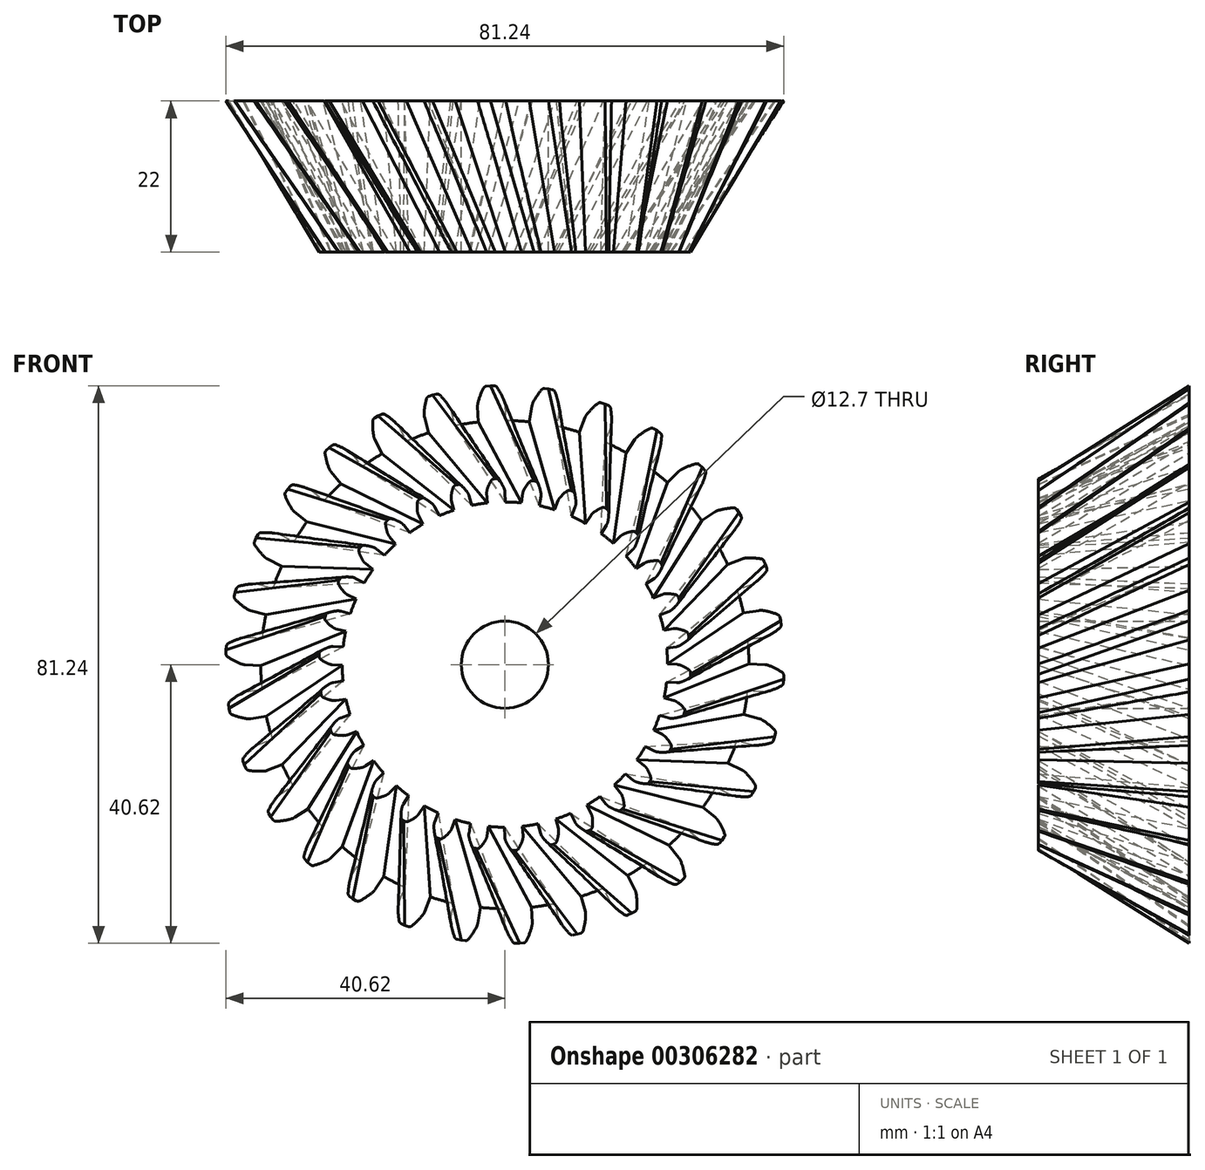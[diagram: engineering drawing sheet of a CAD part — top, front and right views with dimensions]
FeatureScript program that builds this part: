
annotation { "Feature Type Name" : "Feature", "Feature Type Description" : "" }
export const myFeature = defineFeature(function(context is Context, id is Id, definition is map)
    precondition{}
    {
        {
            var Q0;
            Q0=qCreatedBy(makeId("Front.planeOp"),FACE);
            cPlane(context, id + "F0", {"entities" : qUnion([Q0]), "cplaneType" : CPlaneType.OFFSET, "offset" : 22 * mm, "width" : 152.4 * mm, "height" : 152.4 * mm});
        }
        {
            var Q0;
            Q0=qCreatedBy(makeId("Front.planeOp"),FACE);
            var sketch = newSketch(context, id + "F1", { "sketchPlane" : qUnion([Q0])});
            skArc(sketch, "E0", {"start": v(-3.85, 35.35) * mm, "mid": v(-5.56, 35.12) * mm, "end": v(-7.26, 34.81) * mm});
            skArc(sketch, "E1.trimOffspring", {"start": v(-0.08, 38.33) * mm, "mid": v(-0.54, 39.4) * mm, "end": v(-1.12, 40.4) * mm});
            skLineSegment(sketch, "E2", {"start": v(-1.54, 40.62) * mm, "end": v(-2.13, 40.62) * mm});
            skLineSegment(sketch, "E3", {"start": v(0.01, 37.88) * mm, "end": v(0.13, 35.56) * mm});
            skLineSegment(sketch, "E4.MirrorCS", {"start": v(-2.7, 40.56) * mm, "end": v(-2.13, 40.62) * mm});
            skArc(sketch, "E5.MirrorCS", {"start": v(-3.93, 38.13) * mm, "mid": v(-3.58, 39.24) * mm, "end": v(-3.1, 40.3) * mm});
            skLineSegment(sketch, "E6.MirrorCS", {"start": v(-3.97, 37.67) * mm, "end": v(-3.85, 35.35) * mm});
            skPoint(sketch, "E7.visualSharp", {"position": v(-2.98, 40.53) * mm});
            skArc(sketch, "E7.filletArc", {"start": v(-2.7, 40.56) * mm, "mid": v(-2.94, 40.47) * mm, "end": v(-3.1, 40.3) * mm});
            skPoint(sketch, "E8.visualSharp", {"position": v(-1.28, 40.62) * mm});
            skArc(sketch, "E8.filletArc", {"start": v(-1.12, 40.4) * mm, "mid": v(-1.3, 40.56) * mm, "end": v(-1.54, 40.62) * mm});
            skPoint(sketch, "E9.visualSharp", {"position": v(-3.98, 37.9) * mm});
            skArc(sketch, "E9.filletArc", {"start": v(-3.93, 38.13) * mm, "mid": v(-3.97, 37.9) * mm, "end": v(-3.97, 37.67) * mm});
            skPoint(sketch, "E10.visualSharp", {"position": v(0, 38.1) * mm});
            skArc(sketch, "E10.filletArc", {"start": v(0.01, 37.88) * mm, "mid": v(-0.02, 38.1) * mm, "end": v(-0.08, 38.33) * mm});
            skLineSegment(sketch, "E11.1.0", {"start": v(-11.72, 36.02) * mm, "end": v(-11.12, 33.78) * mm});
            skPoint(sketch, "E11.1.1", {"position": v(-11.77, 36.24) * mm});
            skArc(sketch, "E11.1.2", {"start": v(-8.05, 37.48) * mm, "mid": v(-8.72, 38.42) * mm, "end": v(-9.5, 39.28) * mm});
            skArc(sketch, "E11.1.3", {"start": v(-11.77, 36.48) * mm, "mid": v(-11.66, 37.63) * mm, "end": v(-11.42, 38.76) * mm});
            skLineSegment(sketch, "E11.1.4", {"start": v(-9.96, 39.41) * mm, "end": v(-10.53, 39.29) * mm});
            skPoint(sketch, "E11.1.5", {"position": v(-11.34, 39.03) * mm});
            skPoint(sketch, "E11.1.6", {"position": v(-9.7, 39.47) * mm});
            skPoint(sketch, "E11.1.7", {"position": v(-7.92, 37.27) * mm});
            skLineSegment(sketch, "E11.1.8", {"start": v(-7.86, 37.05) * mm, "end": v(-7.26, 34.81) * mm});
            skLineSegment(sketch, "E11.1.9", {"start": v(-11.08, 39.1) * mm, "end": v(-10.53, 39.29) * mm});
            skArc(sketch, "E11.1.10", {"start": v(-11.08, 39.1) * mm, "mid": v(-11.3, 38.98) * mm, "end": v(-11.42, 38.76) * mm});
            skArc(sketch, "E11.1.11", {"start": v(-9.5, 39.28) * mm, "mid": v(-9.7, 39.4) * mm, "end": v(-9.96, 39.41) * mm});
            skArc(sketch, "E11.1.12", {"start": v(-11.77, 36.48) * mm, "mid": v(-11.76, 36.25) * mm, "end": v(-11.72, 36.02) * mm});
            skArc(sketch, "E11.1.13", {"start": v(-7.86, 37.05) * mm, "mid": v(-7.94, 37.27) * mm, "end": v(-8.05, 37.48) * mm});
            skLineSegment(sketch, "E11.2.0", {"start": v(-18.95, 32.8) * mm, "end": v(-17.9, 30.73) * mm});
            skPoint(sketch, "E11.2.1", {"position": v(-19.05, 33) * mm});
            skArc(sketch, "E11.2.2", {"start": v(-15.66, 34.99) * mm, "mid": v(-16.52, 35.77) * mm, "end": v(-17.45, 36.45) * mm});
            skArc(sketch, "E11.2.3", {"start": v(-19.1, 33.24) * mm, "mid": v(-19.23, 34.39) * mm, "end": v(-19.23, 35.54) * mm});
            skLineSegment(sketch, "E11.2.4", {"start": v(-17.93, 36.48) * mm, "end": v(-18.47, 36.24) * mm});
            skPoint(sketch, "E11.2.5", {"position": v(-19.2, 35.82) * mm});
            skPoint(sketch, "E11.2.6", {"position": v(-17.69, 36.59) * mm});
            skPoint(sketch, "E11.2.7", {"position": v(-15.5, 34.8) * mm});
            skLineSegment(sketch, "E11.2.8", {"start": v(-15.4, 34.6) * mm, "end": v(-14.34, 32.54) * mm});
            skLineSegment(sketch, "E11.2.9", {"start": v(-18.97, 35.95) * mm, "end": v(-18.47, 36.24) * mm});
            skArc(sketch, "E11.2.10", {"start": v(-18.97, 35.95) * mm, "mid": v(-19.15, 35.78) * mm, "end": v(-19.23, 35.54) * mm});
            skArc(sketch, "E11.2.11", {"start": v(-17.45, 36.45) * mm, "mid": v(-17.69, 36.52) * mm, "end": v(-17.93, 36.48) * mm});
            skArc(sketch, "E11.2.12", {"start": v(-19.1, 33.24) * mm, "mid": v(-19.04, 33.01) * mm, "end": v(-18.95, 32.8) * mm});
            skArc(sketch, "E11.2.13", {"start": v(-15.4, 34.6) * mm, "mid": v(-15.52, 34.8) * mm, "end": v(-15.66, 34.99) * mm});
            skLineSegment(sketch, "E11.3.0", {"start": v(-25.35, 28.14) * mm, "end": v(-23.9, 26.34) * mm});
            skPoint(sketch, "E11.3.1", {"position": v(-25.5, 28.31) * mm});
            skArc(sketch, "E11.3.2", {"start": v(-22.6, 30.96) * mm, "mid": v(-23.6, 31.55) * mm, "end": v(-24.65, 32.02) * mm});
            skArc(sketch, "E11.3.3", {"start": v(-25.59, 28.54) * mm, "mid": v(-25.96, 29.64) * mm, "end": v(-26.2, 30.77) * mm});
            skLineSegment(sketch, "E11.3.4", {"start": v(-25.13, 31.95) * mm, "end": v(-25.6, 31.61) * mm});
            skPoint(sketch, "E11.3.5", {"position": v(-26.23, 31.04) * mm});
            skPoint(sketch, "E11.3.6", {"position": v(-24.9, 32.11) * mm});
            skPoint(sketch, "E11.3.7", {"position": v(-22.4, 30.82) * mm});
            skLineSegment(sketch, "E11.3.8", {"start": v(-22.25, 30.65) * mm, "end": v(-20.8, 28.85) * mm});
            skLineSegment(sketch, "E11.3.9", {"start": v(-26.03, 31.22) * mm, "end": v(-25.6, 31.61) * mm});
            skArc(sketch, "E11.3.10", {"start": v(-26.03, 31.22) * mm, "mid": v(-26.17, 31.02) * mm, "end": v(-26.2, 30.77) * mm});
            skArc(sketch, "E11.3.11", {"start": v(-24.65, 32.02) * mm, "mid": v(-24.9, 32.05) * mm, "end": v(-25.13, 31.95) * mm});
            skArc(sketch, "E11.3.12", {"start": v(-25.59, 28.54) * mm, "mid": v(-25.49, 28.33) * mm, "end": v(-25.35, 28.14) * mm});
            skArc(sketch, "E11.3.13", {"start": v(-22.25, 30.65) * mm, "mid": v(-22.41, 30.82) * mm, "end": v(-22.6, 30.96) * mm});
            skLineSegment(sketch, "E11.4.0", {"start": v(-30.65, 22.25) * mm, "end": v(-28.85, 20.8) * mm});
            skPoint(sketch, "E11.4.1", {"position": v(-30.82, 22.4) * mm});
            skArc(sketch, "E11.4.2", {"start": v(-28.54, 25.59) * mm, "mid": v(-29.64, 25.96) * mm, "end": v(-30.77, 26.2) * mm});
            skArc(sketch, "E11.4.3", {"start": v(-30.96, 22.6) * mm, "mid": v(-31.55, 23.6) * mm, "end": v(-32.02, 24.65) * mm});
            skLineSegment(sketch, "E11.4.4", {"start": v(-31.22, 26.03) * mm, "end": v(-31.61, 25.6) * mm});
            skPoint(sketch, "E11.4.5", {"position": v(-32.11, 24.9) * mm});
            skPoint(sketch, "E11.4.6", {"position": v(-31.04, 26.23) * mm});
            skPoint(sketch, "E11.4.7", {"position": v(-28.31, 25.5) * mm});
            skLineSegment(sketch, "E11.4.8", {"start": v(-28.14, 25.35) * mm, "end": v(-26.34, 23.9) * mm});
            skLineSegment(sketch, "E11.4.9", {"start": v(-31.95, 25.13) * mm, "end": v(-31.61, 25.6) * mm});
            skArc(sketch, "E11.4.10", {"start": v(-31.95, 25.13) * mm, "mid": v(-32.05, 24.9) * mm, "end": v(-32.02, 24.65) * mm});
            skArc(sketch, "E11.4.11", {"start": v(-30.77, 26.2) * mm, "mid": v(-31.02, 26.17) * mm, "end": v(-31.22, 26.03) * mm});
            skArc(sketch, "E11.4.12", {"start": v(-30.96, 22.6) * mm, "mid": v(-30.82, 22.41) * mm, "end": v(-30.65, 22.25) * mm});
            skArc(sketch, "E11.4.13", {"start": v(-28.14, 25.35) * mm, "mid": v(-28.33, 25.49) * mm, "end": v(-28.54, 25.59) * mm});
            skLineSegment(sketch, "E11.5.0", {"start": v(-34.6, 15.4) * mm, "end": v(-32.54, 14.34) * mm});
            skPoint(sketch, "E11.5.1", {"position": v(-34.8, 15.5) * mm});
            skArc(sketch, "E11.5.2", {"start": v(-33.24, 19.1) * mm, "mid": v(-34.39, 19.23) * mm, "end": v(-35.54, 19.23) * mm});
            skArc(sketch, "E11.5.3", {"start": v(-34.99, 15.66) * mm, "mid": v(-35.77, 16.52) * mm, "end": v(-36.45, 17.45) * mm});
            skLineSegment(sketch, "E11.5.4", {"start": v(-35.95, 18.97) * mm, "end": v(-36.24, 18.47) * mm});
            skPoint(sketch, "E11.5.5", {"position": v(-36.59, 17.69) * mm});
            skPoint(sketch, "E11.5.6", {"position": v(-35.82, 19.2) * mm});
            skPoint(sketch, "E11.5.7", {"position": v(-33, 19.05) * mm});
            skLineSegment(sketch, "E11.5.8", {"start": v(-32.8, 18.95) * mm, "end": v(-30.73, 17.9) * mm});
            skLineSegment(sketch, "E11.5.9", {"start": v(-36.48, 17.93) * mm, "end": v(-36.24, 18.47) * mm});
            skArc(sketch, "E11.5.10", {"start": v(-36.48, 17.93) * mm, "mid": v(-36.52, 17.69) * mm, "end": v(-36.45, 17.45) * mm});
            skArc(sketch, "E11.5.11", {"start": v(-35.54, 19.23) * mm, "mid": v(-35.78, 19.15) * mm, "end": v(-35.95, 18.97) * mm});
            skArc(sketch, "E11.5.12", {"start": v(-34.99, 15.66) * mm, "mid": v(-34.8, 15.52) * mm, "end": v(-34.6, 15.4) * mm});
            skArc(sketch, "E11.5.13", {"start": v(-32.8, 18.95) * mm, "mid": v(-33.01, 19.04) * mm, "end": v(-33.24, 19.1) * mm});
            skLineSegment(sketch, "E11.6.0", {"start": v(-37.05, 7.86) * mm, "end": v(-34.81, 7.26) * mm});
            skPoint(sketch, "E11.6.1", {"position": v(-37.27, 7.92) * mm});
            skArc(sketch, "E11.6.2", {"start": v(-36.48, 11.77) * mm, "mid": v(-37.63, 11.66) * mm, "end": v(-38.76, 11.42) * mm});
            skArc(sketch, "E11.6.3", {"start": v(-37.48, 8.05) * mm, "mid": v(-38.42, 8.72) * mm, "end": v(-39.28, 9.5) * mm});
            skLineSegment(sketch, "E11.6.4", {"start": v(-39.1, 11.08) * mm, "end": v(-39.29, 10.53) * mm});
            skPoint(sketch, "E11.6.5", {"position": v(-39.47, 9.7) * mm});
            skPoint(sketch, "E11.6.6", {"position": v(-39.03, 11.34) * mm});
            skPoint(sketch, "E11.6.7", {"position": v(-36.24, 11.77) * mm});
            skLineSegment(sketch, "E11.6.8", {"start": v(-36.02, 11.72) * mm, "end": v(-33.78, 11.12) * mm});
            skLineSegment(sketch, "E11.6.9", {"start": v(-39.41, 9.96) * mm, "end": v(-39.29, 10.53) * mm});
            skArc(sketch, "E11.6.10", {"start": v(-39.41, 9.96) * mm, "mid": v(-39.4, 9.7) * mm, "end": v(-39.28, 9.5) * mm});
            skArc(sketch, "E11.6.11", {"start": v(-38.76, 11.42) * mm, "mid": v(-38.98, 11.3) * mm, "end": v(-39.1, 11.08) * mm});
            skArc(sketch, "E11.6.12", {"start": v(-37.48, 8.05) * mm, "mid": v(-37.27, 7.94) * mm, "end": v(-37.05, 7.86) * mm});
            skArc(sketch, "E11.6.13", {"start": v(-36.02, 11.72) * mm, "mid": v(-36.25, 11.76) * mm, "end": v(-36.48, 11.77) * mm});
            skLineSegment(sketch, "E11.7.0", {"start": v(-37.88, -0.01) * mm, "end": v(-35.56, -0.13) * mm});
            skPoint(sketch, "E11.7.1", {"position": v(-38.1, 0) * mm});
            skArc(sketch, "E11.7.2", {"start": v(-38.13, 3.93) * mm, "mid": v(-39.24, 3.58) * mm, "end": v(-40.3, 3.1) * mm});
            skArc(sketch, "E11.7.3", {"start": v(-38.33, 0.08) * mm, "mid": v(-39.4, 0.54) * mm, "end": v(-40.4, 1.12) * mm});
            skLineSegment(sketch, "E11.7.4", {"start": v(-40.56, 2.7) * mm, "end": v(-40.62, 2.13) * mm});
            skPoint(sketch, "E11.7.5", {"position": v(-40.62, 1.28) * mm});
            skPoint(sketch, "E11.7.6", {"position": v(-40.53, 2.98) * mm});
            skPoint(sketch, "E11.7.7", {"position": v(-37.9, 3.98) * mm});
            skLineSegment(sketch, "E11.7.8", {"start": v(-37.67, 3.97) * mm, "end": v(-35.35, 3.85) * mm});
            skLineSegment(sketch, "E11.7.9", {"start": v(-40.62, 1.54) * mm, "end": v(-40.62, 2.13) * mm});
            skArc(sketch, "E11.7.10", {"start": v(-40.62, 1.54) * mm, "mid": v(-40.56, 1.3) * mm, "end": v(-40.4, 1.12) * mm});
            skArc(sketch, "E11.7.11", {"start": v(-40.3, 3.1) * mm, "mid": v(-40.47, 2.94) * mm, "end": v(-40.56, 2.7) * mm});
            skArc(sketch, "E11.7.12", {"start": v(-38.33, 0.08) * mm, "mid": v(-38.1, 0.02) * mm, "end": v(-37.88, -0.01) * mm});
            skArc(sketch, "E11.7.13", {"start": v(-37.67, 3.97) * mm, "mid": v(-37.9, 3.97) * mm, "end": v(-38.13, 3.93) * mm});
            skLineSegment(sketch, "E11.8.0", {"start": v(-37.05, -7.89) * mm, "end": v(-34.76, -7.52) * mm});
            skPoint(sketch, "E11.8.1", {"position": v(-37.27, -7.92) * mm});
            skArc(sketch, "E11.8.2", {"start": v(-38.11, -4.09) * mm, "mid": v(-39.12, -4.65) * mm, "end": v(-40.06, -5.34) * mm});
            skArc(sketch, "E11.8.3", {"start": v(-37.51, -7.9) * mm, "mid": v(-38.65, -7.66) * mm, "end": v(-39.74, -7.3) * mm});
            skLineSegment(sketch, "E11.8.4", {"start": v(-40.24, -5.78) * mm, "end": v(-40.17, -6.36) * mm});
            skPoint(sketch, "E11.8.5", {"position": v(-40, -7.2) * mm});
            skPoint(sketch, "E11.8.6", {"position": v(-40.26, -5.52) * mm});
            skPoint(sketch, "E11.8.7", {"position": v(-37.9, -3.98) * mm});
            skLineSegment(sketch, "E11.8.8", {"start": v(-37.67, -3.95) * mm, "end": v(-35.38, -3.58) * mm});
            skLineSegment(sketch, "E11.8.9", {"start": v(-40.05, -6.93) * mm, "end": v(-40.17, -6.36) * mm});
            skArc(sketch, "E11.8.10", {"start": v(-40.05, -6.93) * mm, "mid": v(-39.94, -7.16) * mm, "end": v(-39.74, -7.3) * mm});
            skArc(sketch, "E11.8.11", {"start": v(-40.06, -5.34) * mm, "mid": v(-40.2, -5.54) * mm, "end": v(-40.24, -5.78) * mm});
            skArc(sketch, "E11.8.12", {"start": v(-37.51, -7.9) * mm, "mid": v(-37.28, -7.9) * mm, "end": v(-37.05, -7.89) * mm});
            skArc(sketch, "E11.8.13", {"start": v(-37.67, -3.95) * mm, "mid": v(-37.9, -4) * mm, "end": v(-38.11, -4.09) * mm});
            skLineSegment(sketch, "E11.9.0", {"start": v(-34.6, -15.42) * mm, "end": v(-32.43, -14.59) * mm});
            skPoint(sketch, "E11.9.1", {"position": v(-34.8, -15.5) * mm});
            skArc(sketch, "E11.9.2", {"start": v(-36.43, -11.92) * mm, "mid": v(-37.3, -12.69) * mm, "end": v(-38.07, -13.55) * mm});
            skArc(sketch, "E11.9.3", {"start": v(-35.05, -15.52) * mm, "mid": v(-36.2, -15.53) * mm, "end": v(-37.36, -15.4) * mm});
            skLineSegment(sketch, "E11.9.4", {"start": v(-38.15, -14.02) * mm, "end": v(-37.97, -14.58) * mm});
            skPoint(sketch, "E11.9.5", {"position": v(-37.63, -15.35) * mm});
            skPoint(sketch, "E11.9.6", {"position": v(-38.24, -13.77) * mm});
            skPoint(sketch, "E11.9.7", {"position": v(-36.24, -11.77) * mm});
            skLineSegment(sketch, "E11.9.8", {"start": v(-36.03, -11.7) * mm, "end": v(-33.86, -10.86) * mm});
            skLineSegment(sketch, "E11.9.9", {"start": v(-37.74, -15.11) * mm, "end": v(-37.97, -14.58) * mm});
            skArc(sketch, "E11.9.10", {"start": v(-37.74, -15.11) * mm, "mid": v(-37.58, -15.3) * mm, "end": v(-37.36, -15.4) * mm});
            skArc(sketch, "E11.9.11", {"start": v(-38.07, -13.55) * mm, "mid": v(-38.17, -13.77) * mm, "end": v(-38.15, -14.02) * mm});
            skArc(sketch, "E11.9.12", {"start": v(-35.05, -15.52) * mm, "mid": v(-34.82, -15.48) * mm, "end": v(-34.6, -15.42) * mm});
            skArc(sketch, "E11.9.13", {"start": v(-36.03, -11.7) * mm, "mid": v(-36.24, -11.8) * mm, "end": v(-36.43, -11.92) * mm});
            skLineSegment(sketch, "E11.10.0", {"start": v(-30.64, -22.27) * mm, "end": v(-28.7, -21) * mm});
            skPoint(sketch, "E11.10.1", {"position": v(-30.82, -22.4) * mm});
            skArc(sketch, "E11.10.2", {"start": v(-33.16, -19.24) * mm, "mid": v(-33.85, -20.16) * mm, "end": v(-34.42, -21.17) * mm});
            skArc(sketch, "E11.10.3", {"start": v(-31.06, -22.47) * mm, "mid": v(-32.19, -22.72) * mm, "end": v(-33.34, -22.84) * mm});
            skLineSegment(sketch, "E11.10.4", {"start": v(-34.4, -21.65) * mm, "end": v(-34.11, -22.15) * mm});
            skPoint(sketch, "E11.10.5", {"position": v(-33.61, -22.84) * mm});
            skPoint(sketch, "E11.10.6", {"position": v(-34.54, -21.42) * mm});
            skPoint(sketch, "E11.10.7", {"position": v(-33, -19.05) * mm});
            skLineSegment(sketch, "E11.10.8", {"start": v(-32.8, -18.93) * mm, "end": v(-30.86, -17.66) * mm});
            skLineSegment(sketch, "E11.10.9", {"start": v(-33.77, -22.63) * mm, "end": v(-34.11, -22.15) * mm});
            skArc(sketch, "E11.10.10", {"start": v(-33.77, -22.63) * mm, "mid": v(-33.58, -22.78) * mm, "end": v(-33.34, -22.84) * mm});
            skArc(sketch, "E11.10.11", {"start": v(-34.42, -21.17) * mm, "mid": v(-34.47, -21.41) * mm, "end": v(-34.4, -21.65) * mm});
            skArc(sketch, "E11.10.12", {"start": v(-31.06, -22.47) * mm, "mid": v(-30.84, -22.38) * mm, "end": v(-30.64, -22.27) * mm});
            skArc(sketch, "E11.10.13", {"start": v(-32.8, -18.93) * mm, "mid": v(-33, -19.07) * mm, "end": v(-33.16, -19.24) * mm});
            skLineSegment(sketch, "E11.11.0", {"start": v(-25.34, -28.16) * mm, "end": v(-23.7, -26.52) * mm});
            skPoint(sketch, "E11.11.1", {"position": v(-25.5, -28.31) * mm});
            skArc(sketch, "E11.11.2", {"start": v(-28.43, -25.7) * mm, "mid": v(-28.92, -26.76) * mm, "end": v(-29.27, -27.86) * mm});
            skArc(sketch, "E11.11.3", {"start": v(-25.7, -28.43) * mm, "mid": v(-26.76, -28.92) * mm, "end": v(-27.86, -29.27) * mm});
            skLineSegment(sketch, "E11.11.4", {"start": v(-29.15, -28.33) * mm, "end": v(-28.76, -28.76) * mm});
            skPoint(sketch, "E11.11.5", {"position": v(-28.13, -29.33) * mm});
            skPoint(sketch, "E11.11.6", {"position": v(-29.33, -28.13) * mm});
            skPoint(sketch, "E11.11.7", {"position": v(-28.31, -25.5) * mm});
            skLineSegment(sketch, "E11.11.8", {"start": v(-28.16, -25.34) * mm, "end": v(-26.52, -23.7) * mm});
            skLineSegment(sketch, "E11.11.9", {"start": v(-28.33, -29.15) * mm, "end": v(-28.76, -28.76) * mm});
            skArc(sketch, "E11.11.10", {"start": v(-28.33, -29.15) * mm, "mid": v(-28.1, -29.27) * mm, "end": v(-27.86, -29.27) * mm});
            skArc(sketch, "E11.11.11", {"start": v(-29.27, -27.86) * mm, "mid": v(-29.27, -28.1) * mm, "end": v(-29.15, -28.33) * mm});
            skArc(sketch, "E11.11.12", {"start": v(-25.7, -28.43) * mm, "mid": v(-25.51, -28.3) * mm, "end": v(-25.34, -28.16) * mm});
            skArc(sketch, "E11.11.13", {"start": v(-28.16, -25.34) * mm, "mid": v(-28.3, -25.51) * mm, "end": v(-28.43, -25.7) * mm});
            skLineSegment(sketch, "E11.12.0", {"start": v(-18.93, -32.8) * mm, "end": v(-17.66, -30.86) * mm});
            skPoint(sketch, "E11.12.1", {"position": v(-19.05, -33) * mm});
            skArc(sketch, "E11.12.2", {"start": v(-22.47, -31.06) * mm, "mid": v(-22.72, -32.19) * mm, "end": v(-22.84, -33.34) * mm});
            skArc(sketch, "E11.12.3", {"start": v(-19.24, -33.16) * mm, "mid": v(-20.16, -33.85) * mm, "end": v(-21.17, -34.42) * mm});
            skLineSegment(sketch, "E11.12.4", {"start": v(-22.63, -33.77) * mm, "end": v(-22.15, -34.11) * mm});
            skPoint(sketch, "E11.12.5", {"position": v(-21.42, -34.54) * mm});
            skPoint(sketch, "E11.12.6", {"position": v(-22.84, -33.61) * mm});
            skPoint(sketch, "E11.12.7", {"position": v(-22.4, -30.82) * mm});
            skLineSegment(sketch, "E11.12.8", {"start": v(-22.27, -30.64) * mm, "end": v(-21, -28.7) * mm});
            skLineSegment(sketch, "E11.12.9", {"start": v(-21.65, -34.4) * mm, "end": v(-22.15, -34.11) * mm});
            skArc(sketch, "E11.12.10", {"start": v(-21.65, -34.4) * mm, "mid": v(-21.41, -34.47) * mm, "end": v(-21.17, -34.42) * mm});
            skArc(sketch, "E11.12.11", {"start": v(-22.84, -33.34) * mm, "mid": v(-22.78, -33.58) * mm, "end": v(-22.63, -33.77) * mm});
            skArc(sketch, "E11.12.12", {"start": v(-19.24, -33.16) * mm, "mid": v(-19.07, -33) * mm, "end": v(-18.93, -32.8) * mm});
            skArc(sketch, "E11.12.13", {"start": v(-22.27, -30.64) * mm, "mid": v(-22.38, -30.84) * mm, "end": v(-22.47, -31.06) * mm});
            skLineSegment(sketch, "E11.13.0", {"start": v(-11.7, -36.03) * mm, "end": v(-10.86, -33.86) * mm});
            skPoint(sketch, "E11.13.1", {"position": v(-11.77, -36.24) * mm});
            skArc(sketch, "E11.13.2", {"start": v(-15.52, -35.05) * mm, "mid": v(-15.53, -36.2) * mm, "end": v(-15.4, -37.36) * mm});
            skArc(sketch, "E11.13.3", {"start": v(-11.92, -36.43) * mm, "mid": v(-12.69, -37.3) * mm, "end": v(-13.55, -38.07) * mm});
            skLineSegment(sketch, "E11.13.4", {"start": v(-15.11, -37.74) * mm, "end": v(-14.58, -37.97) * mm});
            skPoint(sketch, "E11.13.5", {"position": v(-13.77, -38.24) * mm});
            skPoint(sketch, "E11.13.6", {"position": v(-15.35, -37.63) * mm});
            skPoint(sketch, "E11.13.7", {"position": v(-15.5, -34.8) * mm});
            skLineSegment(sketch, "E11.13.8", {"start": v(-15.42, -34.6) * mm, "end": v(-14.59, -32.43) * mm});
            skLineSegment(sketch, "E11.13.9", {"start": v(-14.02, -38.15) * mm, "end": v(-14.58, -37.97) * mm});
            skArc(sketch, "E11.13.10", {"start": v(-14.02, -38.15) * mm, "mid": v(-13.77, -38.17) * mm, "end": v(-13.55, -38.07) * mm});
            skArc(sketch, "E11.13.11", {"start": v(-15.4, -37.36) * mm, "mid": v(-15.3, -37.58) * mm, "end": v(-15.11, -37.74) * mm});
            skArc(sketch, "E11.13.12", {"start": v(-11.92, -36.43) * mm, "mid": v(-11.8, -36.24) * mm, "end": v(-11.7, -36.03) * mm});
            skArc(sketch, "E11.13.13", {"start": v(-15.42, -34.6) * mm, "mid": v(-15.48, -34.82) * mm, "end": v(-15.52, -35.05) * mm});
            skLineSegment(sketch, "E11.14.0", {"start": v(-3.95, -37.67) * mm, "end": v(-3.58, -35.38) * mm});
            skPoint(sketch, "E11.14.1", {"position": v(-3.98, -37.9) * mm});
            skArc(sketch, "E11.14.2", {"start": v(-7.9, -37.51) * mm, "mid": v(-7.66, -38.65) * mm, "end": v(-7.3, -39.74) * mm});
            skArc(sketch, "E11.14.3", {"start": v(-4.09, -38.11) * mm, "mid": v(-4.65, -39.12) * mm, "end": v(-5.34, -40.06) * mm});
            skLineSegment(sketch, "E11.14.4", {"start": v(-6.93, -40.05) * mm, "end": v(-6.36, -40.17) * mm});
            skPoint(sketch, "E11.14.5", {"position": v(-5.52, -40.26) * mm});
            skPoint(sketch, "E11.14.6", {"position": v(-7.2, -40) * mm});
            skPoint(sketch, "E11.14.7", {"position": v(-7.92, -37.27) * mm});
            skLineSegment(sketch, "E11.14.8", {"start": v(-7.89, -37.05) * mm, "end": v(-7.52, -34.76) * mm});
            skLineSegment(sketch, "E11.14.9", {"start": v(-5.78, -40.24) * mm, "end": v(-6.36, -40.17) * mm});
            skArc(sketch, "E11.14.10", {"start": v(-5.78, -40.24) * mm, "mid": v(-5.54, -40.2) * mm, "end": v(-5.34, -40.06) * mm});
            skArc(sketch, "E11.14.11", {"start": v(-7.3, -39.74) * mm, "mid": v(-7.16, -39.94) * mm, "end": v(-6.93, -40.05) * mm});
            skArc(sketch, "E11.14.12", {"start": v(-4.09, -38.11) * mm, "mid": v(-4, -37.9) * mm, "end": v(-3.95, -37.67) * mm});
            skArc(sketch, "E11.14.13", {"start": v(-7.89, -37.05) * mm, "mid": v(-7.9, -37.28) * mm, "end": v(-7.9, -37.51) * mm});
            skLineSegment(sketch, "E11.15.0", {"start": v(3.97, -37.67) * mm, "end": v(3.85, -35.35) * mm});
            skPoint(sketch, "E11.15.1", {"position": v(3.98, -37.9) * mm});
            skArc(sketch, "E11.15.2", {"start": v(0.08, -38.33) * mm, "mid": v(0.54, -39.4) * mm, "end": v(1.12, -40.4) * mm});
            skArc(sketch, "E11.15.3", {"start": v(3.93, -38.13) * mm, "mid": v(3.58, -39.24) * mm, "end": v(3.1, -40.3) * mm});
            skLineSegment(sketch, "E11.15.4", {"start": v(1.54, -40.62) * mm, "end": v(2.13, -40.62) * mm});
            skPoint(sketch, "E11.15.5", {"position": v(2.98, -40.53) * mm});
            skPoint(sketch, "E11.15.6", {"position": v(1.28, -40.62) * mm});
            skPoint(sketch, "E11.15.7", {"position": v(0, -38.1) * mm});
            skLineSegment(sketch, "E11.15.8", {"start": v(-0.01, -37.88) * mm, "end": v(-0.13, -35.56) * mm});
            skLineSegment(sketch, "E11.15.9", {"start": v(2.7, -40.56) * mm, "end": v(2.13, -40.62) * mm});
            skArc(sketch, "E11.15.10", {"start": v(2.7, -40.56) * mm, "mid": v(2.94, -40.47) * mm, "end": v(3.1, -40.3) * mm});
            skArc(sketch, "E11.15.11", {"start": v(1.12, -40.4) * mm, "mid": v(1.3, -40.56) * mm, "end": v(1.54, -40.62) * mm});
            skArc(sketch, "E11.15.12", {"start": v(3.93, -38.13) * mm, "mid": v(3.97, -37.9) * mm, "end": v(3.97, -37.67) * mm});
            skArc(sketch, "E11.15.13", {"start": v(-0.01, -37.88) * mm, "mid": v(0.02, -38.1) * mm, "end": v(0.08, -38.33) * mm});
            skLineSegment(sketch, "E11.16.0", {"start": v(11.72, -36.02) * mm, "end": v(11.12, -33.78) * mm});
            skPoint(sketch, "E11.16.1", {"position": v(11.77, -36.24) * mm});
            skArc(sketch, "E11.16.2", {"start": v(8.05, -37.48) * mm, "mid": v(8.72, -38.42) * mm, "end": v(9.5, -39.28) * mm});
            skArc(sketch, "E11.16.3", {"start": v(11.77, -36.48) * mm, "mid": v(11.66, -37.63) * mm, "end": v(11.42, -38.76) * mm});
            skLineSegment(sketch, "E11.16.4", {"start": v(9.96, -39.41) * mm, "end": v(10.53, -39.29) * mm});
            skPoint(sketch, "E11.16.5", {"position": v(11.34, -39.03) * mm});
            skPoint(sketch, "E11.16.6", {"position": v(9.7, -39.47) * mm});
            skPoint(sketch, "E11.16.7", {"position": v(7.92, -37.27) * mm});
            skLineSegment(sketch, "E11.16.8", {"start": v(7.86, -37.05) * mm, "end": v(7.26, -34.81) * mm});
            skLineSegment(sketch, "E11.16.9", {"start": v(11.08, -39.1) * mm, "end": v(10.53, -39.29) * mm});
            skArc(sketch, "E11.16.10", {"start": v(11.08, -39.1) * mm, "mid": v(11.3, -38.98) * mm, "end": v(11.42, -38.76) * mm});
            skArc(sketch, "E11.16.11", {"start": v(9.5, -39.28) * mm, "mid": v(9.7, -39.4) * mm, "end": v(9.96, -39.41) * mm});
            skArc(sketch, "E11.16.12", {"start": v(11.77, -36.48) * mm, "mid": v(11.76, -36.25) * mm, "end": v(11.72, -36.02) * mm});
            skArc(sketch, "E11.16.13", {"start": v(7.86, -37.05) * mm, "mid": v(7.94, -37.27) * mm, "end": v(8.05, -37.48) * mm});
            skLineSegment(sketch, "E11.17.0", {"start": v(18.95, -32.8) * mm, "end": v(17.9, -30.73) * mm});
            skPoint(sketch, "E11.17.1", {"position": v(19.05, -33) * mm});
            skArc(sketch, "E11.17.2", {"start": v(15.66, -34.99) * mm, "mid": v(16.52, -35.77) * mm, "end": v(17.45, -36.45) * mm});
            skArc(sketch, "E11.17.3", {"start": v(19.1, -33.24) * mm, "mid": v(19.23, -34.39) * mm, "end": v(19.23, -35.54) * mm});
            skLineSegment(sketch, "E11.17.4", {"start": v(17.93, -36.48) * mm, "end": v(18.47, -36.24) * mm});
            skPoint(sketch, "E11.17.5", {"position": v(19.2, -35.82) * mm});
            skPoint(sketch, "E11.17.6", {"position": v(17.69, -36.59) * mm});
            skPoint(sketch, "E11.17.7", {"position": v(15.5, -34.8) * mm});
            skLineSegment(sketch, "E11.17.8", {"start": v(15.4, -34.6) * mm, "end": v(14.34, -32.54) * mm});
            skLineSegment(sketch, "E11.17.9", {"start": v(18.97, -35.95) * mm, "end": v(18.47, -36.24) * mm});
            skArc(sketch, "E11.17.10", {"start": v(18.97, -35.95) * mm, "mid": v(19.15, -35.78) * mm, "end": v(19.23, -35.54) * mm});
            skArc(sketch, "E11.17.11", {"start": v(17.45, -36.45) * mm, "mid": v(17.69, -36.52) * mm, "end": v(17.93, -36.48) * mm});
            skArc(sketch, "E11.17.12", {"start": v(19.1, -33.24) * mm, "mid": v(19.04, -33.01) * mm, "end": v(18.95, -32.8) * mm});
            skArc(sketch, "E11.17.13", {"start": v(15.4, -34.6) * mm, "mid": v(15.52, -34.8) * mm, "end": v(15.66, -34.99) * mm});
            skLineSegment(sketch, "E11.18.0", {"start": v(25.35, -28.14) * mm, "end": v(23.9, -26.34) * mm});
            skPoint(sketch, "E11.18.1", {"position": v(25.5, -28.31) * mm});
            skArc(sketch, "E11.18.2", {"start": v(22.6, -30.96) * mm, "mid": v(23.6, -31.55) * mm, "end": v(24.65, -32.02) * mm});
            skArc(sketch, "E11.18.3", {"start": v(25.59, -28.54) * mm, "mid": v(25.96, -29.64) * mm, "end": v(26.2, -30.77) * mm});
            skLineSegment(sketch, "E11.18.4", {"start": v(25.13, -31.95) * mm, "end": v(25.6, -31.61) * mm});
            skPoint(sketch, "E11.18.5", {"position": v(26.23, -31.04) * mm});
            skPoint(sketch, "E11.18.6", {"position": v(24.9, -32.11) * mm});
            skPoint(sketch, "E11.18.7", {"position": v(22.4, -30.82) * mm});
            skLineSegment(sketch, "E11.18.8", {"start": v(22.25, -30.65) * mm, "end": v(20.8, -28.85) * mm});
            skLineSegment(sketch, "E11.18.9", {"start": v(26.03, -31.22) * mm, "end": v(25.6, -31.61) * mm});
            skArc(sketch, "E11.18.10", {"start": v(26.03, -31.22) * mm, "mid": v(26.17, -31.02) * mm, "end": v(26.2, -30.77) * mm});
            skArc(sketch, "E11.18.11", {"start": v(24.65, -32.02) * mm, "mid": v(24.9, -32.05) * mm, "end": v(25.13, -31.95) * mm});
            skArc(sketch, "E11.18.12", {"start": v(25.59, -28.54) * mm, "mid": v(25.49, -28.33) * mm, "end": v(25.35, -28.14) * mm});
            skArc(sketch, "E11.18.13", {"start": v(22.25, -30.65) * mm, "mid": v(22.41, -30.82) * mm, "end": v(22.6, -30.96) * mm});
            skLineSegment(sketch, "E11.19.0", {"start": v(30.65, -22.25) * mm, "end": v(28.85, -20.8) * mm});
            skPoint(sketch, "E11.19.1", {"position": v(30.82, -22.4) * mm});
            skArc(sketch, "E11.19.2", {"start": v(28.54, -25.59) * mm, "mid": v(29.64, -25.96) * mm, "end": v(30.77, -26.2) * mm});
            skArc(sketch, "E11.19.3", {"start": v(30.96, -22.6) * mm, "mid": v(31.55, -23.6) * mm, "end": v(32.02, -24.65) * mm});
            skLineSegment(sketch, "E11.19.4", {"start": v(31.22, -26.03) * mm, "end": v(31.61, -25.6) * mm});
            skPoint(sketch, "E11.19.5", {"position": v(32.11, -24.9) * mm});
            skPoint(sketch, "E11.19.6", {"position": v(31.04, -26.23) * mm});
            skPoint(sketch, "E11.19.7", {"position": v(28.31, -25.5) * mm});
            skLineSegment(sketch, "E11.19.8", {"start": v(28.14, -25.35) * mm, "end": v(26.34, -23.9) * mm});
            skLineSegment(sketch, "E11.19.9", {"start": v(31.95, -25.13) * mm, "end": v(31.61, -25.6) * mm});
            skArc(sketch, "E11.19.10", {"start": v(31.95, -25.13) * mm, "mid": v(32.05, -24.9) * mm, "end": v(32.02, -24.65) * mm});
            skArc(sketch, "E11.19.11", {"start": v(30.77, -26.2) * mm, "mid": v(31.02, -26.17) * mm, "end": v(31.22, -26.03) * mm});
            skArc(sketch, "E11.19.12", {"start": v(30.96, -22.6) * mm, "mid": v(30.82, -22.41) * mm, "end": v(30.65, -22.25) * mm});
            skArc(sketch, "E11.19.13", {"start": v(28.14, -25.35) * mm, "mid": v(28.33, -25.49) * mm, "end": v(28.54, -25.59) * mm});
            skLineSegment(sketch, "E11.20.0", {"start": v(34.6, -15.4) * mm, "end": v(32.54, -14.34) * mm});
            skPoint(sketch, "E11.20.1", {"position": v(34.8, -15.5) * mm});
            skArc(sketch, "E11.20.2", {"start": v(33.24, -19.1) * mm, "mid": v(34.39, -19.23) * mm, "end": v(35.54, -19.23) * mm});
            skArc(sketch, "E11.20.3", {"start": v(34.99, -15.66) * mm, "mid": v(35.77, -16.52) * mm, "end": v(36.45, -17.45) * mm});
            skLineSegment(sketch, "E11.20.4", {"start": v(35.95, -18.97) * mm, "end": v(36.24, -18.47) * mm});
            skPoint(sketch, "E11.20.5", {"position": v(36.59, -17.69) * mm});
            skPoint(sketch, "E11.20.6", {"position": v(35.82, -19.2) * mm});
            skPoint(sketch, "E11.20.7", {"position": v(33, -19.05) * mm});
            skLineSegment(sketch, "E11.20.8", {"start": v(32.8, -18.95) * mm, "end": v(30.73, -17.9) * mm});
            skLineSegment(sketch, "E11.20.9", {"start": v(36.48, -17.93) * mm, "end": v(36.24, -18.47) * mm});
            skArc(sketch, "E11.20.10", {"start": v(36.48, -17.93) * mm, "mid": v(36.52, -17.69) * mm, "end": v(36.45, -17.45) * mm});
            skArc(sketch, "E11.20.11", {"start": v(35.54, -19.23) * mm, "mid": v(35.78, -19.15) * mm, "end": v(35.95, -18.97) * mm});
            skArc(sketch, "E11.20.12", {"start": v(34.99, -15.66) * mm, "mid": v(34.8, -15.52) * mm, "end": v(34.6, -15.4) * mm});
            skArc(sketch, "E11.20.13", {"start": v(32.8, -18.95) * mm, "mid": v(33.01, -19.04) * mm, "end": v(33.24, -19.1) * mm});
            skLineSegment(sketch, "E11.21.0", {"start": v(37.05, -7.86) * mm, "end": v(34.81, -7.26) * mm});
            skPoint(sketch, "E11.21.1", {"position": v(37.27, -7.92) * mm});
            skArc(sketch, "E11.21.2", {"start": v(36.48, -11.77) * mm, "mid": v(37.63, -11.66) * mm, "end": v(38.76, -11.42) * mm});
            skArc(sketch, "E11.21.3", {"start": v(37.48, -8.05) * mm, "mid": v(38.42, -8.72) * mm, "end": v(39.28, -9.5) * mm});
            skLineSegment(sketch, "E11.21.4", {"start": v(39.1, -11.08) * mm, "end": v(39.29, -10.53) * mm});
            skPoint(sketch, "E11.21.5", {"position": v(39.47, -9.7) * mm});
            skPoint(sketch, "E11.21.6", {"position": v(39.03, -11.34) * mm});
            skPoint(sketch, "E11.21.7", {"position": v(36.24, -11.77) * mm});
            skLineSegment(sketch, "E11.21.8", {"start": v(36.02, -11.72) * mm, "end": v(33.78, -11.12) * mm});
            skLineSegment(sketch, "E11.21.9", {"start": v(39.41, -9.96) * mm, "end": v(39.29, -10.53) * mm});
            skArc(sketch, "E11.21.10", {"start": v(39.41, -9.96) * mm, "mid": v(39.4, -9.7) * mm, "end": v(39.28, -9.5) * mm});
            skArc(sketch, "E11.21.11", {"start": v(38.76, -11.42) * mm, "mid": v(38.98, -11.3) * mm, "end": v(39.1, -11.08) * mm});
            skArc(sketch, "E11.21.12", {"start": v(37.48, -8.05) * mm, "mid": v(37.27, -7.94) * mm, "end": v(37.05, -7.86) * mm});
            skArc(sketch, "E11.21.13", {"start": v(36.02, -11.72) * mm, "mid": v(36.25, -11.76) * mm, "end": v(36.48, -11.77) * mm});
            skLineSegment(sketch, "E11.22.0", {"start": v(37.88, 0.01) * mm, "end": v(35.56, 0.13) * mm});
            skPoint(sketch, "E11.22.1", {"position": v(38.1, 0) * mm});
            skArc(sketch, "E11.22.2", {"start": v(38.13, -3.93) * mm, "mid": v(39.24, -3.58) * mm, "end": v(40.3, -3.1) * mm});
            skArc(sketch, "E11.22.3", {"start": v(38.33, -0.08) * mm, "mid": v(39.4, -0.54) * mm, "end": v(40.4, -1.12) * mm});
            skLineSegment(sketch, "E11.22.4", {"start": v(40.56, -2.7) * mm, "end": v(40.62, -2.13) * mm});
            skPoint(sketch, "E11.22.5", {"position": v(40.62, -1.28) * mm});
            skPoint(sketch, "E11.22.6", {"position": v(40.53, -2.98) * mm});
            skPoint(sketch, "E11.22.7", {"position": v(37.9, -3.98) * mm});
            skLineSegment(sketch, "E11.22.8", {"start": v(37.67, -3.97) * mm, "end": v(35.35, -3.85) * mm});
            skLineSegment(sketch, "E11.22.9", {"start": v(40.62, -1.54) * mm, "end": v(40.62, -2.13) * mm});
            skArc(sketch, "E11.22.10", {"start": v(40.62, -1.54) * mm, "mid": v(40.56, -1.3) * mm, "end": v(40.4, -1.12) * mm});
            skArc(sketch, "E11.22.11", {"start": v(40.3, -3.1) * mm, "mid": v(40.47, -2.94) * mm, "end": v(40.56, -2.7) * mm});
            skArc(sketch, "E11.22.12", {"start": v(38.33, -0.08) * mm, "mid": v(38.1, -0.02) * mm, "end": v(37.88, 0.01) * mm});
            skArc(sketch, "E11.22.13", {"start": v(37.67, -3.97) * mm, "mid": v(37.9, -3.97) * mm, "end": v(38.13, -3.93) * mm});
            skLineSegment(sketch, "E11.23.0", {"start": v(37.05, 7.89) * mm, "end": v(34.76, 7.52) * mm});
            skPoint(sketch, "E11.23.1", {"position": v(37.27, 7.92) * mm});
            skArc(sketch, "E11.23.2", {"start": v(38.11, 4.09) * mm, "mid": v(39.12, 4.65) * mm, "end": v(40.06, 5.34) * mm});
            skArc(sketch, "E11.23.3", {"start": v(37.51, 7.9) * mm, "mid": v(38.65, 7.66) * mm, "end": v(39.74, 7.3) * mm});
            skLineSegment(sketch, "E11.23.4", {"start": v(40.24, 5.78) * mm, "end": v(40.17, 6.36) * mm});
            skPoint(sketch, "E11.23.5", {"position": v(40, 7.2) * mm});
            skPoint(sketch, "E11.23.6", {"position": v(40.26, 5.52) * mm});
            skPoint(sketch, "E11.23.7", {"position": v(37.9, 3.98) * mm});
            skLineSegment(sketch, "E11.23.8", {"start": v(37.67, 3.95) * mm, "end": v(35.38, 3.58) * mm});
            skLineSegment(sketch, "E11.23.9", {"start": v(40.05, 6.93) * mm, "end": v(40.17, 6.36) * mm});
            skArc(sketch, "E11.23.10", {"start": v(40.05, 6.93) * mm, "mid": v(39.94, 7.16) * mm, "end": v(39.74, 7.3) * mm});
            skArc(sketch, "E11.23.11", {"start": v(40.06, 5.34) * mm, "mid": v(40.2, 5.54) * mm, "end": v(40.24, 5.78) * mm});
            skArc(sketch, "E11.23.12", {"start": v(37.51, 7.9) * mm, "mid": v(37.28, 7.9) * mm, "end": v(37.05, 7.89) * mm});
            skArc(sketch, "E11.23.13", {"start": v(37.67, 3.95) * mm, "mid": v(37.9, 4) * mm, "end": v(38.11, 4.09) * mm});
            skLineSegment(sketch, "E11.24.0", {"start": v(34.6, 15.42) * mm, "end": v(32.43, 14.59) * mm});
            skPoint(sketch, "E11.24.1", {"position": v(34.8, 15.5) * mm});
            skArc(sketch, "E11.24.2", {"start": v(36.43, 11.92) * mm, "mid": v(37.3, 12.69) * mm, "end": v(38.07, 13.55) * mm});
            skArc(sketch, "E11.24.3", {"start": v(35.05, 15.52) * mm, "mid": v(36.2, 15.53) * mm, "end": v(37.36, 15.4) * mm});
            skLineSegment(sketch, "E11.24.4", {"start": v(38.15, 14.02) * mm, "end": v(37.97, 14.58) * mm});
            skPoint(sketch, "E11.24.5", {"position": v(37.63, 15.35) * mm});
            skPoint(sketch, "E11.24.6", {"position": v(38.24, 13.77) * mm});
            skPoint(sketch, "E11.24.7", {"position": v(36.24, 11.77) * mm});
            skLineSegment(sketch, "E11.24.8", {"start": v(36.03, 11.7) * mm, "end": v(33.86, 10.86) * mm});
            skLineSegment(sketch, "E11.24.9", {"start": v(37.74, 15.11) * mm, "end": v(37.97, 14.58) * mm});
            skArc(sketch, "E11.24.10", {"start": v(37.74, 15.11) * mm, "mid": v(37.58, 15.3) * mm, "end": v(37.36, 15.4) * mm});
            skArc(sketch, "E11.24.11", {"start": v(38.07, 13.55) * mm, "mid": v(38.17, 13.77) * mm, "end": v(38.15, 14.02) * mm});
            skArc(sketch, "E11.24.12", {"start": v(35.05, 15.52) * mm, "mid": v(34.82, 15.48) * mm, "end": v(34.6, 15.42) * mm});
            skArc(sketch, "E11.24.13", {"start": v(36.03, 11.7) * mm, "mid": v(36.24, 11.8) * mm, "end": v(36.43, 11.92) * mm});
            skLineSegment(sketch, "E11.25.0", {"start": v(30.64, 22.27) * mm, "end": v(28.7, 21) * mm});
            skPoint(sketch, "E11.25.1", {"position": v(30.82, 22.4) * mm});
            skArc(sketch, "E11.25.2", {"start": v(33.16, 19.24) * mm, "mid": v(33.85, 20.16) * mm, "end": v(34.42, 21.17) * mm});
            skArc(sketch, "E11.25.3", {"start": v(31.06, 22.47) * mm, "mid": v(32.19, 22.72) * mm, "end": v(33.34, 22.84) * mm});
            skLineSegment(sketch, "E11.25.4", {"start": v(34.4, 21.65) * mm, "end": v(34.11, 22.15) * mm});
            skPoint(sketch, "E11.25.5", {"position": v(33.61, 22.84) * mm});
            skPoint(sketch, "E11.25.6", {"position": v(34.54, 21.42) * mm});
            skPoint(sketch, "E11.25.7", {"position": v(33, 19.05) * mm});
            skLineSegment(sketch, "E11.25.8", {"start": v(32.8, 18.93) * mm, "end": v(30.86, 17.66) * mm});
            skLineSegment(sketch, "E11.25.9", {"start": v(33.77, 22.63) * mm, "end": v(34.11, 22.15) * mm});
            skArc(sketch, "E11.25.10", {"start": v(33.77, 22.63) * mm, "mid": v(33.58, 22.78) * mm, "end": v(33.34, 22.84) * mm});
            skArc(sketch, "E11.25.11", {"start": v(34.42, 21.17) * mm, "mid": v(34.47, 21.41) * mm, "end": v(34.4, 21.65) * mm});
            skArc(sketch, "E11.25.12", {"start": v(31.06, 22.47) * mm, "mid": v(30.84, 22.38) * mm, "end": v(30.64, 22.27) * mm});
            skArc(sketch, "E11.25.13", {"start": v(32.8, 18.93) * mm, "mid": v(33, 19.07) * mm, "end": v(33.16, 19.24) * mm});
            skLineSegment(sketch, "E11.26.0", {"start": v(25.34, 28.16) * mm, "end": v(23.7, 26.52) * mm});
            skPoint(sketch, "E11.26.1", {"position": v(25.5, 28.31) * mm});
            skArc(sketch, "E11.26.2", {"start": v(28.43, 25.7) * mm, "mid": v(28.92, 26.76) * mm, "end": v(29.27, 27.86) * mm});
            skArc(sketch, "E11.26.3", {"start": v(25.7, 28.43) * mm, "mid": v(26.76, 28.92) * mm, "end": v(27.86, 29.27) * mm});
            skLineSegment(sketch, "E11.26.4", {"start": v(29.15, 28.33) * mm, "end": v(28.76, 28.76) * mm});
            skPoint(sketch, "E11.26.5", {"position": v(28.13, 29.33) * mm});
            skPoint(sketch, "E11.26.6", {"position": v(29.33, 28.13) * mm});
            skPoint(sketch, "E11.26.7", {"position": v(28.31, 25.5) * mm});
            skLineSegment(sketch, "E11.26.8", {"start": v(28.16, 25.34) * mm, "end": v(26.52, 23.7) * mm});
            skLineSegment(sketch, "E11.26.9", {"start": v(28.33, 29.15) * mm, "end": v(28.76, 28.76) * mm});
            skArc(sketch, "E11.26.10", {"start": v(28.33, 29.15) * mm, "mid": v(28.1, 29.27) * mm, "end": v(27.86, 29.27) * mm});
            skArc(sketch, "E11.26.11", {"start": v(29.27, 27.86) * mm, "mid": v(29.27, 28.1) * mm, "end": v(29.15, 28.33) * mm});
            skArc(sketch, "E11.26.12", {"start": v(25.7, 28.43) * mm, "mid": v(25.51, 28.3) * mm, "end": v(25.34, 28.16) * mm});
            skArc(sketch, "E11.26.13", {"start": v(28.16, 25.34) * mm, "mid": v(28.3, 25.51) * mm, "end": v(28.43, 25.7) * mm});
            skLineSegment(sketch, "E11.27.0", {"start": v(18.93, 32.8) * mm, "end": v(17.66, 30.86) * mm});
            skPoint(sketch, "E11.27.1", {"position": v(19.05, 33) * mm});
            skArc(sketch, "E11.27.2", {"start": v(22.47, 31.06) * mm, "mid": v(22.72, 32.19) * mm, "end": v(22.84, 33.34) * mm});
            skArc(sketch, "E11.27.3", {"start": v(19.24, 33.16) * mm, "mid": v(20.16, 33.85) * mm, "end": v(21.17, 34.42) * mm});
            skLineSegment(sketch, "E11.27.4", {"start": v(22.63, 33.77) * mm, "end": v(22.15, 34.11) * mm});
            skPoint(sketch, "E11.27.5", {"position": v(21.42, 34.54) * mm});
            skPoint(sketch, "E11.27.6", {"position": v(22.84, 33.61) * mm});
            skPoint(sketch, "E11.27.7", {"position": v(22.4, 30.82) * mm});
            skLineSegment(sketch, "E11.27.8", {"start": v(22.27, 30.64) * mm, "end": v(21, 28.7) * mm});
            skLineSegment(sketch, "E11.27.9", {"start": v(21.65, 34.4) * mm, "end": v(22.15, 34.11) * mm});
            skArc(sketch, "E11.27.10", {"start": v(21.65, 34.4) * mm, "mid": v(21.41, 34.47) * mm, "end": v(21.17, 34.42) * mm});
            skArc(sketch, "E11.27.11", {"start": v(22.84, 33.34) * mm, "mid": v(22.78, 33.58) * mm, "end": v(22.63, 33.77) * mm});
            skArc(sketch, "E11.27.12", {"start": v(19.24, 33.16) * mm, "mid": v(19.07, 33) * mm, "end": v(18.93, 32.8) * mm});
            skArc(sketch, "E11.27.13", {"start": v(22.27, 30.64) * mm, "mid": v(22.38, 30.84) * mm, "end": v(22.47, 31.06) * mm});
            skLineSegment(sketch, "E11.28.0", {"start": v(11.7, 36.03) * mm, "end": v(10.86, 33.86) * mm});
            skPoint(sketch, "E11.28.1", {"position": v(11.77, 36.24) * mm});
            skArc(sketch, "E11.28.2", {"start": v(15.52, 35.05) * mm, "mid": v(15.53, 36.2) * mm, "end": v(15.4, 37.36) * mm});
            skArc(sketch, "E11.28.3", {"start": v(11.92, 36.43) * mm, "mid": v(12.69, 37.3) * mm, "end": v(13.55, 38.07) * mm});
            skLineSegment(sketch, "E11.28.4", {"start": v(15.11, 37.74) * mm, "end": v(14.58, 37.97) * mm});
            skPoint(sketch, "E11.28.5", {"position": v(13.77, 38.24) * mm});
            skPoint(sketch, "E11.28.6", {"position": v(15.35, 37.63) * mm});
            skPoint(sketch, "E11.28.7", {"position": v(15.5, 34.8) * mm});
            skLineSegment(sketch, "E11.28.8", {"start": v(15.42, 34.6) * mm, "end": v(14.59, 32.43) * mm});
            skLineSegment(sketch, "E11.28.9", {"start": v(14.02, 38.15) * mm, "end": v(14.58, 37.97) * mm});
            skArc(sketch, "E11.28.10", {"start": v(14.02, 38.15) * mm, "mid": v(13.77, 38.17) * mm, "end": v(13.55, 38.07) * mm});
            skArc(sketch, "E11.28.11", {"start": v(15.4, 37.36) * mm, "mid": v(15.3, 37.58) * mm, "end": v(15.11, 37.74) * mm});
            skArc(sketch, "E11.28.12", {"start": v(11.92, 36.43) * mm, "mid": v(11.8, 36.24) * mm, "end": v(11.7, 36.03) * mm});
            skArc(sketch, "E11.28.13", {"start": v(15.42, 34.6) * mm, "mid": v(15.48, 34.82) * mm, "end": v(15.52, 35.05) * mm});
            skLineSegment(sketch, "E11.29.0", {"start": v(3.95, 37.67) * mm, "end": v(3.58, 35.38) * mm});
            skPoint(sketch, "E11.29.1", {"position": v(3.98, 37.9) * mm});
            skArc(sketch, "E11.29.2", {"start": v(7.9, 37.51) * mm, "mid": v(7.66, 38.65) * mm, "end": v(7.3, 39.74) * mm});
            skArc(sketch, "E11.29.3", {"start": v(4.09, 38.11) * mm, "mid": v(4.65, 39.12) * mm, "end": v(5.34, 40.06) * mm});
            skLineSegment(sketch, "E11.29.4", {"start": v(6.93, 40.05) * mm, "end": v(6.36, 40.17) * mm});
            skPoint(sketch, "E11.29.5", {"position": v(5.52, 40.26) * mm});
            skPoint(sketch, "E11.29.6", {"position": v(7.2, 40) * mm});
            skPoint(sketch, "E11.29.7", {"position": v(7.92, 37.27) * mm});
            skLineSegment(sketch, "E11.29.8", {"start": v(7.89, 37.05) * mm, "end": v(7.52, 34.76) * mm});
            skLineSegment(sketch, "E11.29.9", {"start": v(5.78, 40.24) * mm, "end": v(6.36, 40.17) * mm});
            skArc(sketch, "E11.29.10", {"start": v(5.78, 40.24) * mm, "mid": v(5.54, 40.2) * mm, "end": v(5.34, 40.06) * mm});
            skArc(sketch, "E11.29.11", {"start": v(7.3, 39.74) * mm, "mid": v(7.16, 39.94) * mm, "end": v(6.93, 40.05) * mm});
            skArc(sketch, "E11.29.12", {"start": v(4.09, 38.11) * mm, "mid": v(4, 37.9) * mm, "end": v(3.95, 37.67) * mm});
            skArc(sketch, "E11.29.13", {"start": v(7.89, 37.05) * mm, "mid": v(7.9, 37.28) * mm, "end": v(7.9, 37.51) * mm});
            skArc(sketch, "E12.trimOffspring", {"start": v(-11.12, 33.78) * mm, "mid": v(-12.74, 33.2) * mm, "end": v(-14.34, 32.54) * mm});
            skArc(sketch, "E13.trimOffspring", {"start": v(-17.9, 30.73) * mm, "mid": v(-19.37, 29.82) * mm, "end": v(-20.8, 28.85) * mm});
            skArc(sketch, "E14.trimOffspring", {"start": v(-23.9, 26.34) * mm, "mid": v(-25.14, 25.14) * mm, "end": v(-26.34, 23.9) * mm});
            skArc(sketch, "E15.trimOffspring", {"start": v(-28.85, 20.8) * mm, "mid": v(-29.82, 19.37) * mm, "end": v(-30.73, 17.9) * mm});
            skArc(sketch, "E16.trimOffspring", {"start": v(-32.54, 14.34) * mm, "mid": v(-33.2, 12.74) * mm, "end": v(-33.78, 11.12) * mm});
            skArc(sketch, "E17.trimOffspring", {"start": v(-34.81, 7.26) * mm, "mid": v(-35.12, 5.56) * mm, "end": v(-35.35, 3.85) * mm});
            skArc(sketch, "E18.trimOffspring", {"start": v(-35.56, -0.13) * mm, "mid": v(-35.51, -1.86) * mm, "end": v(-35.38, -3.58) * mm});
            skArc(sketch, "E19.trimOffspring", {"start": v(-34.76, -7.52) * mm, "mid": v(-34.35, -9.2) * mm, "end": v(-33.86, -10.86) * mm});
            skArc(sketch, "E20.trimOffspring", {"start": v(-32.43, -14.59) * mm, "mid": v(-31.68, -16.14) * mm, "end": v(-30.86, -17.66) * mm});
            skArc(sketch, "E21.trimOffspring", {"start": v(-28.7, -21) * mm, "mid": v(-27.64, -22.38) * mm, "end": v(-26.52, -23.7) * mm});
            skArc(sketch, "E22.trimOffspring", {"start": v(-23.7, -26.52) * mm, "mid": v(-22.38, -27.64) * mm, "end": v(-21, -28.7) * mm});
            skArc(sketch, "E23.trimOffspring", {"start": v(-17.66, -30.86) * mm, "mid": v(-16.14, -31.68) * mm, "end": v(-14.59, -32.43) * mm});
            skArc(sketch, "E24.trimOffspring", {"start": v(-10.86, -33.86) * mm, "mid": v(-9.2, -34.35) * mm, "end": v(-7.52, -34.76) * mm});
            skArc(sketch, "E25.trimOffspring", {"start": v(-3.58, -35.38) * mm, "mid": v(-1.86, -35.51) * mm, "end": v(-0.13, -35.56) * mm});
            skArc(sketch, "E26.trimOffspring", {"start": v(3.85, -35.35) * mm, "mid": v(5.56, -35.12) * mm, "end": v(7.26, -34.81) * mm});
            skArc(sketch, "E27.trimOffspring", {"start": v(11.12, -33.78) * mm, "mid": v(12.74, -33.2) * mm, "end": v(14.34, -32.54) * mm});
            skArc(sketch, "E28.trimOffspring", {"start": v(17.9, -30.73) * mm, "mid": v(19.37, -29.82) * mm, "end": v(20.8, -28.85) * mm});
            skArc(sketch, "E29.trimOffspring", {"start": v(23.9, -26.34) * mm, "mid": v(25.14, -25.14) * mm, "end": v(26.34, -23.9) * mm});
            skArc(sketch, "E30.trimOffspring", {"start": v(28.85, -20.8) * mm, "mid": v(29.82, -19.37) * mm, "end": v(30.73, -17.9) * mm});
            skArc(sketch, "E31.trimOffspring", {"start": v(32.54, -14.34) * mm, "mid": v(33.2, -12.74) * mm, "end": v(33.78, -11.12) * mm});
            skArc(sketch, "E32.trimOffspring", {"start": v(34.81, -7.26) * mm, "mid": v(35.12, -5.56) * mm, "end": v(35.35, -3.85) * mm});
            skArc(sketch, "E33.trimOffspring", {"start": v(35.56, 0.13) * mm, "mid": v(35.51, 1.86) * mm, "end": v(35.38, 3.58) * mm});
            skArc(sketch, "E34.trimOffspring", {"start": v(34.76, 7.52) * mm, "mid": v(34.35, 9.2) * mm, "end": v(33.86, 10.86) * mm});
            skArc(sketch, "E35.trimOffspring", {"start": v(32.43, 14.59) * mm, "mid": v(31.68, 16.14) * mm, "end": v(30.86, 17.66) * mm});
            skArc(sketch, "E36.trimOffspring", {"start": v(28.7, 21) * mm, "mid": v(27.64, 22.38) * mm, "end": v(26.52, 23.7) * mm});
            skArc(sketch, "E37.trimOffspring", {"start": v(23.7, 26.52) * mm, "mid": v(22.38, 27.64) * mm, "end": v(21, 28.7) * mm});
            skArc(sketch, "E38.trimOffspring", {"start": v(17.66, 30.86) * mm, "mid": v(16.14, 31.68) * mm, "end": v(14.59, 32.43) * mm});
            skArc(sketch, "E39.trimOffspring", {"start": v(10.86, 33.86) * mm, "mid": v(9.2, 34.35) * mm, "end": v(7.52, 34.76) * mm});
            skArc(sketch, "E40.trimOffspring", {"start": v(3.58, 35.38) * mm, "mid": v(1.86, 35.51) * mm, "end": v(0.13, 35.56) * mm});
            skSolve(sketch);
        }
        {
            var Q0;
            Q0=qCreatedBy(id+"F0.planeOp",FACE);
            var sketch = newSketch(context, id + "F2", { "sketchPlane" : qUnion([Q0])});
            skArc(sketch, "E41", {"start": v(-2.57, 23.56) * mm, "mid": v(-3.7, 23.4) * mm, "end": v(-4.84, 23.2) * mm});
            skArc(sketch, "E42.trimOffspring", {"start": v(-0.12, 25.69) * mm, "mid": v(-0.43, 26.3) * mm, "end": v(-0.8, 26.86) * mm});
            skLineSegment(sketch, "E43", {"start": v(0.01, 25.13) * mm, "end": v(0.09, 23.7) * mm});
            skLineSegment(sketch, "E44", {"start": v(-1.2, 27.07) * mm, "end": v(-1.42, 27.07) * mm});
            skLineSegment(sketch, "E45.MirrorCS", {"start": v(-1.63, 27.05) * mm, "end": v(-1.42, 27.07) * mm});
            skArc(sketch, "E46.MirrorCS", {"start": v(-2.57, 25.56) * mm, "mid": v(-2.32, 26.2) * mm, "end": v(-2.02, 26.8) * mm});
            skLineSegment(sketch, "E47.MirrorCS", {"start": v(-2.64, 25) * mm, "end": v(-2.57, 23.56) * mm});
            skPoint(sketch, "E48.visualSharp", {"position": v(0, 25.4) * mm});
            skArc(sketch, "E48.filletArc", {"start": v(0.01, 25.13) * mm, "mid": v(-0.03, 25.42) * mm, "end": v(-0.12, 25.69) * mm});
            skPoint(sketch, "E49.visualSharp", {"position": v(-2.66, 25.26) * mm});
            skArc(sketch, "E49.filletArc", {"start": v(-2.57, 25.56) * mm, "mid": v(-2.63, 25.28) * mm, "end": v(-2.64, 25) * mm});
            skPoint(sketch, "E50.visualSharp", {"position": v(-1.88, 27.02) * mm});
            skArc(sketch, "E50.filletArc", {"start": v(-1.63, 27.05) * mm, "mid": v(-1.85, 26.97) * mm, "end": v(-2.02, 26.8) * mm});
            skPoint(sketch, "E51.visualSharp", {"position": v(-0.96, 27.07) * mm});
            skArc(sketch, "E51.filletArc", {"start": v(-0.8, 26.86) * mm, "mid": v(-0.98, 27.02) * mm, "end": v(-1.2, 27.07) * mm});
            skPoint(sketch, "E52.1.0", {"position": v(-7.46, 26.04) * mm});
            skArc(sketch, "E52.1.1", {"start": v(-5.46, 25.1) * mm, "mid": v(-5.88, 25.63) * mm, "end": v(-6.37, 26.11) * mm});
            skLineSegment(sketch, "E52.1.2", {"start": v(-5.21, 24.58) * mm, "end": v(-4.84, 23.2) * mm});
            skPoint(sketch, "E52.1.3", {"position": v(-5.28, 24.84) * mm});
            skPoint(sketch, "E52.1.4", {"position": v(-7.85, 24.16) * mm});
            skArc(sketch, "E52.1.5", {"start": v(-7.82, 24.47) * mm, "mid": v(-7.72, 25.14) * mm, "end": v(-7.54, 25.8) * mm});
            skPoint(sketch, "E52.1.6", {"position": v(-6.56, 26.28) * mm});
            skArc(sketch, "E52.1.7", {"start": v(-6.37, 26.11) * mm, "mid": v(-6.57, 26.22) * mm, "end": v(-6.8, 26.23) * mm});
            skArc(sketch, "E52.1.8", {"start": v(-7.82, 24.47) * mm, "mid": v(-7.83, 24.18) * mm, "end": v(-7.78, 23.9) * mm});
            skArc(sketch, "E52.1.9", {"start": v(-5.21, 24.58) * mm, "mid": v(-5.31, 24.85) * mm, "end": v(-5.46, 25.1) * mm});
            skLineSegment(sketch, "E52.1.10", {"start": v(-7.78, 23.9) * mm, "end": v(-7.4, 22.51) * mm});
            skArc(sketch, "E52.1.11", {"start": v(-7.22, 26.12) * mm, "mid": v(-7.42, 26) * mm, "end": v(-7.54, 25.8) * mm});
            skLineSegment(sketch, "E52.1.12", {"start": v(-6.8, 26.23) * mm, "end": v(-7.02, 26.19) * mm});
            skLineSegment(sketch, "E52.1.13", {"start": v(-7.22, 26.12) * mm, "end": v(-7.02, 26.19) * mm});
            skPoint(sketch, "E52.2.0", {"position": v(-12.7, 23.92) * mm});
            skArc(sketch, "E52.2.1", {"start": v(-10.56, 23.42) * mm, "mid": v(-11.08, 23.85) * mm, "end": v(-11.65, 24.22) * mm});
            skLineSegment(sketch, "E52.2.2", {"start": v(-10.2, 22.96) * mm, "end": v(-9.56, 21.69) * mm});
            skPoint(sketch, "E52.2.3", {"position": v(-10.33, 23.2) * mm});
            skPoint(sketch, "E52.2.4", {"position": v(-12.7, 22) * mm});
            skArc(sketch, "E52.2.5", {"start": v(-12.74, 22.3) * mm, "mid": v(-12.78, 22.98) * mm, "end": v(-12.74, 23.66) * mm});
            skPoint(sketch, "E52.2.6", {"position": v(-11.88, 24.34) * mm});
            skArc(sketch, "E52.2.7", {"start": v(-11.65, 24.22) * mm, "mid": v(-11.88, 24.28) * mm, "end": v(-12.11, 24.24) * mm});
            skArc(sketch, "E52.2.8", {"start": v(-12.74, 22.3) * mm, "mid": v(-12.68, 22.02) * mm, "end": v(-12.58, 21.76) * mm});
            skArc(sketch, "E52.2.9", {"start": v(-10.2, 22.96) * mm, "mid": v(-10.36, 23.2) * mm, "end": v(-10.56, 23.42) * mm});
            skLineSegment(sketch, "E52.2.10", {"start": v(-12.58, 21.76) * mm, "end": v(-11.93, 20.48) * mm});
            skArc(sketch, "E52.2.11", {"start": v(-12.5, 24.05) * mm, "mid": v(-12.66, 23.89) * mm, "end": v(-12.74, 23.66) * mm});
            skLineSegment(sketch, "E52.2.12", {"start": v(-12.11, 24.24) * mm, "end": v(-12.3, 24.15) * mm});
            skLineSegment(sketch, "E52.2.13", {"start": v(-12.5, 24.05) * mm, "end": v(-12.3, 24.15) * mm});
            skPoint(sketch, "E52.3.0", {"position": v(-17.4, 20.76) * mm});
            skArc(sketch, "E52.3.1", {"start": v(-15.2, 20.71) * mm, "mid": v(-15.8, 21.02) * mm, "end": v(-16.44, 21.26) * mm});
            skLineSegment(sketch, "E52.3.2", {"start": v(-14.76, 20.34) * mm, "end": v(-13.86, 19.22) * mm});
            skPoint(sketch, "E52.3.3", {"position": v(-14.93, 20.55) * mm});
            skPoint(sketch, "E52.3.4", {"position": v(-17, 18.88) * mm});
            skArc(sketch, "E52.3.5", {"start": v(-17.1, 19.17) * mm, "mid": v(-17.28, 19.83) * mm, "end": v(-17.38, 20.5) * mm});
            skPoint(sketch, "E52.3.6", {"position": v(-16.69, 21.34) * mm});
            skArc(sketch, "E52.3.7", {"start": v(-16.44, 21.26) * mm, "mid": v(-16.67, 21.28) * mm, "end": v(-16.89, 21.2) * mm});
            skArc(sketch, "E52.3.8", {"start": v(-17.1, 19.17) * mm, "mid": v(-16.99, 18.9) * mm, "end": v(-16.83, 18.67) * mm});
            skArc(sketch, "E52.3.9", {"start": v(-14.76, 20.34) * mm, "mid": v(-14.96, 20.55) * mm, "end": v(-15.2, 20.71) * mm});
            skLineSegment(sketch, "E52.3.10", {"start": v(-16.83, 18.67) * mm, "end": v(-15.92, 17.55) * mm});
            skArc(sketch, "E52.3.11", {"start": v(-17.22, 20.93) * mm, "mid": v(-17.35, 20.73) * mm, "end": v(-17.38, 20.5) * mm});
            skLineSegment(sketch, "E52.3.12", {"start": v(-16.89, 21.2) * mm, "end": v(-17.06, 21.07) * mm});
            skLineSegment(sketch, "E52.3.13", {"start": v(-17.22, 20.93) * mm, "end": v(-17.06, 21.07) * mm});
            skPoint(sketch, "E52.4.0", {"position": v(-21.34, 16.69) * mm});
            skArc(sketch, "E52.4.1", {"start": v(-19.17, 17.1) * mm, "mid": v(-19.83, 17.28) * mm, "end": v(-20.5, 17.38) * mm});
            skLineSegment(sketch, "E52.4.2", {"start": v(-18.67, 16.83) * mm, "end": v(-17.55, 15.92) * mm});
            skPoint(sketch, "E52.4.3", {"position": v(-18.88, 17) * mm});
            skPoint(sketch, "E52.4.4", {"position": v(-20.55, 14.93) * mm});
            skArc(sketch, "E52.4.5", {"start": v(-20.71, 15.2) * mm, "mid": v(-21.02, 15.8) * mm, "end": v(-21.26, 16.44) * mm});
            skPoint(sketch, "E52.4.6", {"position": v(-20.76, 17.4) * mm});
            skArc(sketch, "E52.4.7", {"start": v(-20.5, 17.38) * mm, "mid": v(-20.73, 17.35) * mm, "end": v(-20.93, 17.22) * mm});
            skArc(sketch, "E52.4.8", {"start": v(-20.71, 15.2) * mm, "mid": v(-20.55, 14.96) * mm, "end": v(-20.34, 14.76) * mm});
            skArc(sketch, "E52.4.9", {"start": v(-18.67, 16.83) * mm, "mid": v(-18.9, 16.99) * mm, "end": v(-19.17, 17.1) * mm});
            skLineSegment(sketch, "E52.4.10", {"start": v(-20.34, 14.76) * mm, "end": v(-19.22, 13.86) * mm});
            skArc(sketch, "E52.4.11", {"start": v(-21.2, 16.89) * mm, "mid": v(-21.28, 16.67) * mm, "end": v(-21.26, 16.44) * mm});
            skLineSegment(sketch, "E52.4.12", {"start": v(-20.93, 17.22) * mm, "end": v(-21.07, 17.06) * mm});
            skLineSegment(sketch, "E52.4.13", {"start": v(-21.2, 16.89) * mm, "end": v(-21.07, 17.06) * mm});
            skPoint(sketch, "E52.5.0", {"position": v(-24.34, 11.88) * mm});
            skArc(sketch, "E52.5.1", {"start": v(-22.3, 12.74) * mm, "mid": v(-22.98, 12.78) * mm, "end": v(-23.66, 12.74) * mm});
            skLineSegment(sketch, "E52.5.2", {"start": v(-21.76, 12.58) * mm, "end": v(-20.48, 11.93) * mm});
            skPoint(sketch, "E52.5.3", {"position": v(-22, 12.7) * mm});
            skPoint(sketch, "E52.5.4", {"position": v(-23.2, 10.33) * mm});
            skArc(sketch, "E52.5.5", {"start": v(-23.42, 10.56) * mm, "mid": v(-23.85, 11.08) * mm, "end": v(-24.22, 11.65) * mm});
            skPoint(sketch, "E52.5.6", {"position": v(-23.92, 12.7) * mm});
            skArc(sketch, "E52.5.7", {"start": v(-23.66, 12.74) * mm, "mid": v(-23.89, 12.66) * mm, "end": v(-24.05, 12.5) * mm});
            skArc(sketch, "E52.5.8", {"start": v(-23.42, 10.56) * mm, "mid": v(-23.2, 10.36) * mm, "end": v(-22.96, 10.2) * mm});
            skArc(sketch, "E52.5.9", {"start": v(-21.76, 12.58) * mm, "mid": v(-22.02, 12.68) * mm, "end": v(-22.3, 12.74) * mm});
            skLineSegment(sketch, "E52.5.10", {"start": v(-22.96, 10.2) * mm, "end": v(-21.69, 9.56) * mm});
            skArc(sketch, "E52.5.11", {"start": v(-24.24, 12.11) * mm, "mid": v(-24.28, 11.88) * mm, "end": v(-24.22, 11.65) * mm});
            skLineSegment(sketch, "E52.5.12", {"start": v(-24.05, 12.5) * mm, "end": v(-24.15, 12.3) * mm});
            skLineSegment(sketch, "E52.5.13", {"start": v(-24.24, 12.11) * mm, "end": v(-24.15, 12.3) * mm});
            skPoint(sketch, "E52.6.0", {"position": v(-26.28, 6.56) * mm});
            skArc(sketch, "E52.6.1", {"start": v(-24.47, 7.82) * mm, "mid": v(-25.14, 7.72) * mm, "end": v(-25.8, 7.54) * mm});
            skLineSegment(sketch, "E52.6.2", {"start": v(-23.9, 7.78) * mm, "end": v(-22.51, 7.4) * mm});
            skPoint(sketch, "E52.6.3", {"position": v(-24.16, 7.85) * mm});
            skPoint(sketch, "E52.6.4", {"position": v(-24.84, 5.28) * mm});
            skArc(sketch, "E52.6.5", {"start": v(-25.1, 5.46) * mm, "mid": v(-25.63, 5.88) * mm, "end": v(-26.11, 6.37) * mm});
            skPoint(sketch, "E52.6.6", {"position": v(-26.04, 7.46) * mm});
            skArc(sketch, "E52.6.7", {"start": v(-25.8, 7.54) * mm, "mid": v(-26, 7.42) * mm, "end": v(-26.12, 7.22) * mm});
            skArc(sketch, "E52.6.8", {"start": v(-25.1, 5.46) * mm, "mid": v(-24.85, 5.31) * mm, "end": v(-24.58, 5.21) * mm});
            skArc(sketch, "E52.6.9", {"start": v(-23.9, 7.78) * mm, "mid": v(-24.18, 7.83) * mm, "end": v(-24.47, 7.82) * mm});
            skLineSegment(sketch, "E52.6.10", {"start": v(-24.58, 5.21) * mm, "end": v(-23.2, 4.84) * mm});
            skArc(sketch, "E52.6.11", {"start": v(-26.23, 6.8) * mm, "mid": v(-26.22, 6.57) * mm, "end": v(-26.11, 6.37) * mm});
            skLineSegment(sketch, "E52.6.12", {"start": v(-26.12, 7.22) * mm, "end": v(-26.19, 7.02) * mm});
            skLineSegment(sketch, "E52.6.13", {"start": v(-26.23, 6.8) * mm, "end": v(-26.19, 7.02) * mm});
            skPoint(sketch, "E52.7.0", {"position": v(-27.07, 0.96) * mm});
            skArc(sketch, "E52.7.1", {"start": v(-25.56, 2.57) * mm, "mid": v(-26.2, 2.32) * mm, "end": v(-26.8, 2.02) * mm});
            skLineSegment(sketch, "E52.7.2", {"start": v(-25, 2.64) * mm, "end": v(-23.56, 2.57) * mm});
            skPoint(sketch, "E52.7.3", {"position": v(-25.26, 2.66) * mm});
            skPoint(sketch, "E52.7.4", {"position": v(-25.4, 0) * mm});
            skArc(sketch, "E52.7.5", {"start": v(-25.69, 0.12) * mm, "mid": v(-26.3, 0.43) * mm, "end": v(-26.86, 0.8) * mm});
            skPoint(sketch, "E52.7.6", {"position": v(-27.02, 1.88) * mm});
            skArc(sketch, "E52.7.7", {"start": v(-26.8, 2.02) * mm, "mid": v(-26.97, 1.85) * mm, "end": v(-27.05, 1.63) * mm});
            skArc(sketch, "E52.7.8", {"start": v(-25.69, 0.12) * mm, "mid": v(-25.42, 0.03) * mm, "end": v(-25.13, -0.01) * mm});
            skArc(sketch, "E52.7.9", {"start": v(-25, 2.64) * mm, "mid": v(-25.28, 2.63) * mm, "end": v(-25.56, 2.57) * mm});
            skLineSegment(sketch, "E52.7.10", {"start": v(-25.13, -0.01) * mm, "end": v(-23.7, -0.09) * mm});
            skArc(sketch, "E52.7.11", {"start": v(-27.07, 1.2) * mm, "mid": v(-27.02, 0.98) * mm, "end": v(-26.86, 0.8) * mm});
            skLineSegment(sketch, "E52.7.12", {"start": v(-27.05, 1.63) * mm, "end": v(-27.07, 1.42) * mm});
            skLineSegment(sketch, "E52.7.13", {"start": v(-27.07, 1.2) * mm, "end": v(-27.07, 1.42) * mm});
            skPoint(sketch, "E52.8.0", {"position": v(-26.68, -4.7) * mm});
            skArc(sketch, "E52.8.1", {"start": v(-25.54, -2.8) * mm, "mid": v(-26.1, -3.17) * mm, "end": v(-26.63, -3.6) * mm});
            skLineSegment(sketch, "E52.8.2", {"start": v(-25, -2.61) * mm, "end": v(-23.58, -2.39) * mm});
            skPoint(sketch, "E52.8.3", {"position": v(-25.26, -2.66) * mm});
            skPoint(sketch, "E52.8.4", {"position": v(-24.84, -5.28) * mm});
            skArc(sketch, "E52.8.5", {"start": v(-25.15, -5.22) * mm, "mid": v(-25.8, -5.05) * mm, "end": v(-26.44, -4.8) * mm});
            skPoint(sketch, "E52.8.6", {"position": v(-26.82, -3.78) * mm});
            skArc(sketch, "E52.8.7", {"start": v(-26.63, -3.6) * mm, "mid": v(-26.77, -3.8) * mm, "end": v(-26.8, -4.03) * mm});
            skArc(sketch, "E52.8.8", {"start": v(-25.15, -5.22) * mm, "mid": v(-24.87, -5.26) * mm, "end": v(-24.58, -5.24) * mm});
            skArc(sketch, "E52.8.9", {"start": v(-25, -2.61) * mm, "mid": v(-25.27, -2.68) * mm, "end": v(-25.54, -2.8) * mm});
            skLineSegment(sketch, "E52.8.10", {"start": v(-24.58, -5.24) * mm, "end": v(-23.16, -5.01) * mm});
            skArc(sketch, "E52.8.11", {"start": v(-26.73, -4.45) * mm, "mid": v(-26.63, -4.66) * mm, "end": v(-26.44, -4.8) * mm});
            skLineSegment(sketch, "E52.8.12", {"start": v(-26.8, -4.03) * mm, "end": v(-26.78, -4.24) * mm});
            skLineSegment(sketch, "E52.8.13", {"start": v(-26.73, -4.45) * mm, "end": v(-26.78, -4.24) * mm});
            skPoint(sketch, "E52.9.0", {"position": v(-25.12, -10.14) * mm});
            skArc(sketch, "E52.9.1", {"start": v(-24.4, -8.05) * mm, "mid": v(-24.88, -8.53) * mm, "end": v(-25.3, -9.06) * mm});
            skLineSegment(sketch, "E52.9.2", {"start": v(-23.9, -7.75) * mm, "end": v(-22.57, -7.24) * mm});
            skPoint(sketch, "E52.9.3", {"position": v(-24.16, -7.85) * mm});
            skPoint(sketch, "E52.9.4", {"position": v(-23.2, -10.33) * mm});
            skArc(sketch, "E52.9.5", {"start": v(-23.52, -10.34) * mm, "mid": v(-24.2, -10.3) * mm, "end": v(-24.87, -10.2) * mm});
            skPoint(sketch, "E52.9.6", {"position": v(-25.45, -9.28) * mm});
            skArc(sketch, "E52.9.7", {"start": v(-25.3, -9.06) * mm, "mid": v(-25.4, -9.28) * mm, "end": v(-25.37, -9.51) * mm});
            skArc(sketch, "E52.9.8", {"start": v(-23.52, -10.34) * mm, "mid": v(-23.23, -10.31) * mm, "end": v(-22.95, -10.23) * mm});
            skArc(sketch, "E52.9.9", {"start": v(-23.9, -7.75) * mm, "mid": v(-24.16, -7.88) * mm, "end": v(-24.4, -8.05) * mm});
            skLineSegment(sketch, "E52.9.10", {"start": v(-22.95, -10.23) * mm, "end": v(-21.61, -9.72) * mm});
            skArc(sketch, "E52.9.11", {"start": v(-25.22, -9.9) * mm, "mid": v(-25.08, -10.1) * mm, "end": v(-24.87, -10.2) * mm});
            skLineSegment(sketch, "E52.9.12", {"start": v(-25.37, -9.51) * mm, "end": v(-25.3, -9.72) * mm});
            skLineSegment(sketch, "E52.9.13", {"start": v(-25.22, -9.9) * mm, "end": v(-25.3, -9.72) * mm});
            skPoint(sketch, "E52.10.0", {"position": v(-22.46, -15.14) * mm});
            skArc(sketch, "E52.10.1", {"start": v(-22.19, -12.95) * mm, "mid": v(-22.56, -13.52) * mm, "end": v(-22.87, -14.12) * mm});
            skLineSegment(sketch, "E52.10.2", {"start": v(-21.77, -12.55) * mm, "end": v(-20.57, -11.77) * mm});
            skPoint(sketch, "E52.10.3", {"position": v(-22, -12.7) * mm});
            skPoint(sketch, "E52.10.4", {"position": v(-20.55, -14.93) * mm});
            skArc(sketch, "E52.10.5", {"start": v(-20.85, -15) * mm, "mid": v(-21.52, -15.11) * mm, "end": v(-22.2, -15.15) * mm});
            skPoint(sketch, "E52.10.6", {"position": v(-22.97, -14.36) * mm});
            skArc(sketch, "E52.10.7", {"start": v(-22.87, -14.12) * mm, "mid": v(-22.9, -14.36) * mm, "end": v(-22.84, -14.58) * mm});
            skArc(sketch, "E52.10.8", {"start": v(-20.85, -15) * mm, "mid": v(-20.58, -14.92) * mm, "end": v(-20.32, -14.78) * mm});
            skArc(sketch, "E52.10.9", {"start": v(-21.77, -12.55) * mm, "mid": v(-22, -12.73) * mm, "end": v(-22.19, -12.95) * mm});
            skLineSegment(sketch, "E52.10.10", {"start": v(-20.32, -14.78) * mm, "end": v(-19.12, -14) * mm});
            skArc(sketch, "E52.10.11", {"start": v(-22.61, -14.94) * mm, "mid": v(-22.43, -15.09) * mm, "end": v(-22.2, -15.15) * mm});
            skLineSegment(sketch, "E52.10.12", {"start": v(-22.84, -14.58) * mm, "end": v(-22.74, -14.76) * mm});
            skLineSegment(sketch, "E52.10.13", {"start": v(-22.61, -14.94) * mm, "end": v(-22.74, -14.76) * mm});
            skPoint(sketch, "E52.11.0", {"position": v(-18.83, -19.48) * mm});
            skArc(sketch, "E52.11.1", {"start": v(-19.01, -17.28) * mm, "mid": v(-19.25, -17.91) * mm, "end": v(-19.43, -18.57) * mm});
            skLineSegment(sketch, "E52.11.2", {"start": v(-18.68, -16.8) * mm, "end": v(-17.67, -15.8) * mm});
            skPoint(sketch, "E52.11.3", {"position": v(-18.88, -17) * mm});
            skPoint(sketch, "E52.11.4", {"position": v(-17, -18.88) * mm});
            skArc(sketch, "E52.11.5", {"start": v(-17.28, -19.01) * mm, "mid": v(-17.91, -19.25) * mm, "end": v(-18.57, -19.43) * mm});
            skPoint(sketch, "E52.11.6", {"position": v(-19.48, -18.83) * mm});
            skArc(sketch, "E52.11.7", {"start": v(-19.43, -18.57) * mm, "mid": v(-19.42, -18.8) * mm, "end": v(-19.31, -19.01) * mm});
            skArc(sketch, "E52.11.8", {"start": v(-17.28, -19.01) * mm, "mid": v(-17.03, -18.87) * mm, "end": v(-16.8, -18.68) * mm});
            skArc(sketch, "E52.11.9", {"start": v(-18.68, -16.8) * mm, "mid": v(-18.87, -17.03) * mm, "end": v(-19.01, -17.28) * mm});
            skLineSegment(sketch, "E52.11.10", {"start": v(-16.8, -18.68) * mm, "end": v(-15.8, -17.67) * mm});
            skArc(sketch, "E52.11.11", {"start": v(-19.01, -19.31) * mm, "mid": v(-18.8, -19.42) * mm, "end": v(-18.57, -19.43) * mm});
            skLineSegment(sketch, "E52.11.12", {"start": v(-19.31, -19.01) * mm, "end": v(-19.17, -19.17) * mm});
            skLineSegment(sketch, "E52.11.13", {"start": v(-19.01, -19.31) * mm, "end": v(-19.17, -19.17) * mm});
            skPoint(sketch, "E52.12.0", {"position": v(-14.36, -22.97) * mm});
            skArc(sketch, "E52.12.1", {"start": v(-15, -20.85) * mm, "mid": v(-15.11, -21.52) * mm, "end": v(-15.15, -22.2) * mm});
            skLineSegment(sketch, "E52.12.2", {"start": v(-14.78, -20.32) * mm, "end": v(-14, -19.12) * mm});
            skPoint(sketch, "E52.12.3", {"position": v(-14.93, -20.55) * mm});
            skPoint(sketch, "E52.12.4", {"position": v(-12.7, -22) * mm});
            skArc(sketch, "E52.12.5", {"start": v(-12.95, -22.19) * mm, "mid": v(-13.52, -22.56) * mm, "end": v(-14.12, -22.87) * mm});
            skPoint(sketch, "E52.12.6", {"position": v(-15.14, -22.46) * mm});
            skArc(sketch, "E52.12.7", {"start": v(-15.15, -22.2) * mm, "mid": v(-15.09, -22.43) * mm, "end": v(-14.94, -22.61) * mm});
            skArc(sketch, "E52.12.8", {"start": v(-12.95, -22.19) * mm, "mid": v(-12.73, -22) * mm, "end": v(-12.55, -21.77) * mm});
            skArc(sketch, "E52.12.9", {"start": v(-14.78, -20.32) * mm, "mid": v(-14.92, -20.58) * mm, "end": v(-15, -20.85) * mm});
            skLineSegment(sketch, "E52.12.10", {"start": v(-12.55, -21.77) * mm, "end": v(-11.77, -20.57) * mm});
            skArc(sketch, "E52.12.11", {"start": v(-14.58, -22.84) * mm, "mid": v(-14.36, -22.9) * mm, "end": v(-14.12, -22.87) * mm});
            skLineSegment(sketch, "E52.12.12", {"start": v(-14.94, -22.61) * mm, "end": v(-14.76, -22.74) * mm});
            skLineSegment(sketch, "E52.12.13", {"start": v(-14.58, -22.84) * mm, "end": v(-14.76, -22.74) * mm});
            skPoint(sketch, "E52.13.0", {"position": v(-9.28, -25.45) * mm});
            skArc(sketch, "E52.13.1", {"start": v(-10.34, -23.52) * mm, "mid": v(-10.3, -24.2) * mm, "end": v(-10.2, -24.87) * mm});
            skLineSegment(sketch, "E52.13.2", {"start": v(-10.23, -22.95) * mm, "end": v(-9.72, -21.61) * mm});
            skPoint(sketch, "E52.13.3", {"position": v(-10.33, -23.2) * mm});
            skPoint(sketch, "E52.13.4", {"position": v(-7.85, -24.16) * mm});
            skArc(sketch, "E52.13.5", {"start": v(-8.05, -24.4) * mm, "mid": v(-8.53, -24.88) * mm, "end": v(-9.06, -25.3) * mm});
            skPoint(sketch, "E52.13.6", {"position": v(-10.14, -25.12) * mm});
            skArc(sketch, "E52.13.7", {"start": v(-10.2, -24.87) * mm, "mid": v(-10.1, -25.08) * mm, "end": v(-9.9, -25.22) * mm});
            skArc(sketch, "E52.13.8", {"start": v(-8.05, -24.4) * mm, "mid": v(-7.88, -24.16) * mm, "end": v(-7.75, -23.9) * mm});
            skArc(sketch, "E52.13.9", {"start": v(-10.23, -22.95) * mm, "mid": v(-10.31, -23.23) * mm, "end": v(-10.34, -23.52) * mm});
            skLineSegment(sketch, "E52.13.10", {"start": v(-7.75, -23.9) * mm, "end": v(-7.24, -22.57) * mm});
            skArc(sketch, "E52.13.11", {"start": v(-9.51, -25.37) * mm, "mid": v(-9.28, -25.4) * mm, "end": v(-9.06, -25.3) * mm});
            skLineSegment(sketch, "E52.13.12", {"start": v(-9.9, -25.22) * mm, "end": v(-9.72, -25.3) * mm});
            skLineSegment(sketch, "E52.13.13", {"start": v(-9.51, -25.37) * mm, "end": v(-9.72, -25.3) * mm});
            skPoint(sketch, "E52.14.0", {"position": v(-3.78, -26.82) * mm});
            skArc(sketch, "E52.14.1", {"start": v(-5.22, -25.15) * mm, "mid": v(-5.05, -25.8) * mm, "end": v(-4.8, -26.44) * mm});
            skLineSegment(sketch, "E52.14.2", {"start": v(-5.24, -24.58) * mm, "end": v(-5.01, -23.16) * mm});
            skPoint(sketch, "E52.14.3", {"position": v(-5.28, -24.84) * mm});
            skPoint(sketch, "E52.14.4", {"position": v(-2.66, -25.26) * mm});
            skArc(sketch, "E52.14.5", {"start": v(-2.8, -25.54) * mm, "mid": v(-3.17, -26.1) * mm, "end": v(-3.6, -26.63) * mm});
            skPoint(sketch, "E52.14.6", {"position": v(-4.7, -26.68) * mm});
            skArc(sketch, "E52.14.7", {"start": v(-4.8, -26.44) * mm, "mid": v(-4.66, -26.63) * mm, "end": v(-4.45, -26.73) * mm});
            skArc(sketch, "E52.14.8", {"start": v(-2.8, -25.54) * mm, "mid": v(-2.68, -25.27) * mm, "end": v(-2.61, -25) * mm});
            skArc(sketch, "E52.14.9", {"start": v(-5.24, -24.58) * mm, "mid": v(-5.26, -24.87) * mm, "end": v(-5.22, -25.15) * mm});
            skLineSegment(sketch, "E52.14.10", {"start": v(-2.61, -25) * mm, "end": v(-2.39, -23.58) * mm});
            skArc(sketch, "E52.14.11", {"start": v(-4.03, -26.8) * mm, "mid": v(-3.8, -26.77) * mm, "end": v(-3.6, -26.63) * mm});
            skLineSegment(sketch, "E52.14.12", {"start": v(-4.45, -26.73) * mm, "end": v(-4.24, -26.78) * mm});
            skLineSegment(sketch, "E52.14.13", {"start": v(-4.03, -26.8) * mm, "end": v(-4.24, -26.78) * mm});
            skPoint(sketch, "E52.15.0", {"position": v(1.88, -27.02) * mm});
            skArc(sketch, "E52.15.1", {"start": v(0.12, -25.69) * mm, "mid": v(0.43, -26.3) * mm, "end": v(0.8, -26.86) * mm});
            skLineSegment(sketch, "E52.15.2", {"start": v(-0.01, -25.13) * mm, "end": v(-0.09, -23.7) * mm});
            skPoint(sketch, "E52.15.3", {"position": v(0, -25.4) * mm});
            skPoint(sketch, "E52.15.4", {"position": v(2.66, -25.26) * mm});
            skArc(sketch, "E52.15.5", {"start": v(2.57, -25.56) * mm, "mid": v(2.32, -26.2) * mm, "end": v(2.02, -26.8) * mm});
            skPoint(sketch, "E52.15.6", {"position": v(0.96, -27.07) * mm});
            skArc(sketch, "E52.15.7", {"start": v(0.8, -26.86) * mm, "mid": v(0.98, -27.02) * mm, "end": v(1.2, -27.07) * mm});
            skArc(sketch, "E52.15.8", {"start": v(2.57, -25.56) * mm, "mid": v(2.63, -25.28) * mm, "end": v(2.64, -25) * mm});
            skArc(sketch, "E52.15.9", {"start": v(-0.01, -25.13) * mm, "mid": v(0.03, -25.42) * mm, "end": v(0.12, -25.69) * mm});
            skLineSegment(sketch, "E52.15.10", {"start": v(2.64, -25) * mm, "end": v(2.57, -23.56) * mm});
            skArc(sketch, "E52.15.11", {"start": v(1.63, -27.05) * mm, "mid": v(1.85, -26.97) * mm, "end": v(2.02, -26.8) * mm});
            skLineSegment(sketch, "E52.15.12", {"start": v(1.2, -27.07) * mm, "end": v(1.42, -27.07) * mm});
            skLineSegment(sketch, "E52.15.13", {"start": v(1.63, -27.05) * mm, "end": v(1.42, -27.07) * mm});
            skPoint(sketch, "E52.16.0", {"position": v(7.46, -26.04) * mm});
            skArc(sketch, "E52.16.1", {"start": v(5.46, -25.1) * mm, "mid": v(5.88, -25.63) * mm, "end": v(6.37, -26.11) * mm});
            skLineSegment(sketch, "E52.16.2", {"start": v(5.21, -24.58) * mm, "end": v(4.84, -23.2) * mm});
            skPoint(sketch, "E52.16.3", {"position": v(5.28, -24.84) * mm});
            skPoint(sketch, "E52.16.4", {"position": v(7.85, -24.16) * mm});
            skArc(sketch, "E52.16.5", {"start": v(7.82, -24.47) * mm, "mid": v(7.72, -25.14) * mm, "end": v(7.54, -25.8) * mm});
            skPoint(sketch, "E52.16.6", {"position": v(6.56, -26.28) * mm});
            skArc(sketch, "E52.16.7", {"start": v(6.37, -26.11) * mm, "mid": v(6.57, -26.22) * mm, "end": v(6.8, -26.23) * mm});
            skArc(sketch, "E52.16.8", {"start": v(7.82, -24.47) * mm, "mid": v(7.83, -24.18) * mm, "end": v(7.78, -23.9) * mm});
            skArc(sketch, "E52.16.9", {"start": v(5.21, -24.58) * mm, "mid": v(5.31, -24.85) * mm, "end": v(5.46, -25.1) * mm});
            skLineSegment(sketch, "E52.16.10", {"start": v(7.78, -23.9) * mm, "end": v(7.4, -22.51) * mm});
            skArc(sketch, "E52.16.11", {"start": v(7.22, -26.12) * mm, "mid": v(7.42, -26) * mm, "end": v(7.54, -25.8) * mm});
            skLineSegment(sketch, "E52.16.12", {"start": v(6.8, -26.23) * mm, "end": v(7.02, -26.19) * mm});
            skLineSegment(sketch, "E52.16.13", {"start": v(7.22, -26.12) * mm, "end": v(7.02, -26.19) * mm});
            skPoint(sketch, "E52.17.0", {"position": v(12.7, -23.92) * mm});
            skArc(sketch, "E52.17.1", {"start": v(10.56, -23.42) * mm, "mid": v(11.08, -23.85) * mm, "end": v(11.65, -24.22) * mm});
            skLineSegment(sketch, "E52.17.2", {"start": v(10.2, -22.96) * mm, "end": v(9.56, -21.69) * mm});
            skPoint(sketch, "E52.17.3", {"position": v(10.33, -23.2) * mm});
            skPoint(sketch, "E52.17.4", {"position": v(12.7, -22) * mm});
            skArc(sketch, "E52.17.5", {"start": v(12.74, -22.3) * mm, "mid": v(12.78, -22.98) * mm, "end": v(12.74, -23.66) * mm});
            skPoint(sketch, "E52.17.6", {"position": v(11.88, -24.34) * mm});
            skArc(sketch, "E52.17.7", {"start": v(11.65, -24.22) * mm, "mid": v(11.88, -24.28) * mm, "end": v(12.11, -24.24) * mm});
            skArc(sketch, "E52.17.8", {"start": v(12.74, -22.3) * mm, "mid": v(12.68, -22.02) * mm, "end": v(12.58, -21.76) * mm});
            skArc(sketch, "E52.17.9", {"start": v(10.2, -22.96) * mm, "mid": v(10.36, -23.2) * mm, "end": v(10.56, -23.42) * mm});
            skLineSegment(sketch, "E52.17.10", {"start": v(12.58, -21.76) * mm, "end": v(11.93, -20.48) * mm});
            skArc(sketch, "E52.17.11", {"start": v(12.5, -24.05) * mm, "mid": v(12.66, -23.89) * mm, "end": v(12.74, -23.66) * mm});
            skLineSegment(sketch, "E52.17.12", {"start": v(12.11, -24.24) * mm, "end": v(12.3, -24.15) * mm});
            skLineSegment(sketch, "E52.17.13", {"start": v(12.5, -24.05) * mm, "end": v(12.3, -24.15) * mm});
            skPoint(sketch, "E52.18.0", {"position": v(17.4, -20.76) * mm});
            skArc(sketch, "E52.18.1", {"start": v(15.2, -20.71) * mm, "mid": v(15.8, -21.02) * mm, "end": v(16.44, -21.26) * mm});
            skLineSegment(sketch, "E52.18.2", {"start": v(14.76, -20.34) * mm, "end": v(13.86, -19.22) * mm});
            skPoint(sketch, "E52.18.3", {"position": v(14.93, -20.55) * mm});
            skPoint(sketch, "E52.18.4", {"position": v(17, -18.88) * mm});
            skArc(sketch, "E52.18.5", {"start": v(17.1, -19.17) * mm, "mid": v(17.28, -19.83) * mm, "end": v(17.38, -20.5) * mm});
            skPoint(sketch, "E52.18.6", {"position": v(16.69, -21.34) * mm});
            skArc(sketch, "E52.18.7", {"start": v(16.44, -21.26) * mm, "mid": v(16.67, -21.28) * mm, "end": v(16.89, -21.2) * mm});
            skArc(sketch, "E52.18.8", {"start": v(17.1, -19.17) * mm, "mid": v(16.99, -18.9) * mm, "end": v(16.83, -18.67) * mm});
            skArc(sketch, "E52.18.9", {"start": v(14.76, -20.34) * mm, "mid": v(14.96, -20.55) * mm, "end": v(15.2, -20.71) * mm});
            skLineSegment(sketch, "E52.18.10", {"start": v(16.83, -18.67) * mm, "end": v(15.92, -17.55) * mm});
            skArc(sketch, "E52.18.11", {"start": v(17.22, -20.93) * mm, "mid": v(17.35, -20.73) * mm, "end": v(17.38, -20.5) * mm});
            skLineSegment(sketch, "E52.18.12", {"start": v(16.89, -21.2) * mm, "end": v(17.06, -21.07) * mm});
            skLineSegment(sketch, "E52.18.13", {"start": v(17.22, -20.93) * mm, "end": v(17.06, -21.07) * mm});
            skPoint(sketch, "E52.19.0", {"position": v(21.34, -16.69) * mm});
            skArc(sketch, "E52.19.1", {"start": v(19.17, -17.1) * mm, "mid": v(19.83, -17.28) * mm, "end": v(20.5, -17.38) * mm});
            skLineSegment(sketch, "E52.19.2", {"start": v(18.67, -16.83) * mm, "end": v(17.55, -15.92) * mm});
            skPoint(sketch, "E52.19.3", {"position": v(18.88, -17) * mm});
            skPoint(sketch, "E52.19.4", {"position": v(20.55, -14.93) * mm});
            skArc(sketch, "E52.19.5", {"start": v(20.71, -15.2) * mm, "mid": v(21.02, -15.8) * mm, "end": v(21.26, -16.44) * mm});
            skPoint(sketch, "E52.19.6", {"position": v(20.76, -17.4) * mm});
            skArc(sketch, "E52.19.7", {"start": v(20.5, -17.38) * mm, "mid": v(20.73, -17.35) * mm, "end": v(20.93, -17.22) * mm});
            skArc(sketch, "E52.19.8", {"start": v(20.71, -15.2) * mm, "mid": v(20.55, -14.96) * mm, "end": v(20.34, -14.76) * mm});
            skArc(sketch, "E52.19.9", {"start": v(18.67, -16.83) * mm, "mid": v(18.9, -16.99) * mm, "end": v(19.17, -17.1) * mm});
            skLineSegment(sketch, "E52.19.10", {"start": v(20.34, -14.76) * mm, "end": v(19.22, -13.86) * mm});
            skArc(sketch, "E52.19.11", {"start": v(21.2, -16.89) * mm, "mid": v(21.28, -16.67) * mm, "end": v(21.26, -16.44) * mm});
            skLineSegment(sketch, "E52.19.12", {"start": v(20.93, -17.22) * mm, "end": v(21.07, -17.06) * mm});
            skLineSegment(sketch, "E52.19.13", {"start": v(21.2, -16.89) * mm, "end": v(21.07, -17.06) * mm});
            skPoint(sketch, "E52.20.0", {"position": v(24.34, -11.88) * mm});
            skArc(sketch, "E52.20.1", {"start": v(22.3, -12.74) * mm, "mid": v(22.98, -12.78) * mm, "end": v(23.66, -12.74) * mm});
            skLineSegment(sketch, "E52.20.2", {"start": v(21.76, -12.58) * mm, "end": v(20.48, -11.93) * mm});
            skPoint(sketch, "E52.20.3", {"position": v(22, -12.7) * mm});
            skPoint(sketch, "E52.20.4", {"position": v(23.2, -10.33) * mm});
            skArc(sketch, "E52.20.5", {"start": v(23.42, -10.56) * mm, "mid": v(23.85, -11.08) * mm, "end": v(24.22, -11.65) * mm});
            skPoint(sketch, "E52.20.6", {"position": v(23.92, -12.7) * mm});
            skArc(sketch, "E52.20.7", {"start": v(23.66, -12.74) * mm, "mid": v(23.89, -12.66) * mm, "end": v(24.05, -12.5) * mm});
            skArc(sketch, "E52.20.8", {"start": v(23.42, -10.56) * mm, "mid": v(23.2, -10.36) * mm, "end": v(22.96, -10.2) * mm});
            skArc(sketch, "E52.20.9", {"start": v(21.76, -12.58) * mm, "mid": v(22.02, -12.68) * mm, "end": v(22.3, -12.74) * mm});
            skLineSegment(sketch, "E52.20.10", {"start": v(22.96, -10.2) * mm, "end": v(21.69, -9.56) * mm});
            skArc(sketch, "E52.20.11", {"start": v(24.24, -12.11) * mm, "mid": v(24.28, -11.88) * mm, "end": v(24.22, -11.65) * mm});
            skLineSegment(sketch, "E52.20.12", {"start": v(24.05, -12.5) * mm, "end": v(24.15, -12.3) * mm});
            skLineSegment(sketch, "E52.20.13", {"start": v(24.24, -12.11) * mm, "end": v(24.15, -12.3) * mm});
            skPoint(sketch, "E52.21.0", {"position": v(26.28, -6.56) * mm});
            skArc(sketch, "E52.21.1", {"start": v(24.47, -7.82) * mm, "mid": v(25.14, -7.72) * mm, "end": v(25.8, -7.54) * mm});
            skLineSegment(sketch, "E52.21.2", {"start": v(23.9, -7.78) * mm, "end": v(22.51, -7.4) * mm});
            skPoint(sketch, "E52.21.3", {"position": v(24.16, -7.85) * mm});
            skPoint(sketch, "E52.21.4", {"position": v(24.84, -5.28) * mm});
            skArc(sketch, "E52.21.5", {"start": v(25.1, -5.46) * mm, "mid": v(25.63, -5.88) * mm, "end": v(26.11, -6.37) * mm});
            skPoint(sketch, "E52.21.6", {"position": v(26.04, -7.46) * mm});
            skArc(sketch, "E52.21.7", {"start": v(25.8, -7.54) * mm, "mid": v(26, -7.42) * mm, "end": v(26.12, -7.22) * mm});
            skArc(sketch, "E52.21.8", {"start": v(25.1, -5.46) * mm, "mid": v(24.85, -5.31) * mm, "end": v(24.58, -5.21) * mm});
            skArc(sketch, "E52.21.9", {"start": v(23.9, -7.78) * mm, "mid": v(24.18, -7.83) * mm, "end": v(24.47, -7.82) * mm});
            skLineSegment(sketch, "E52.21.10", {"start": v(24.58, -5.21) * mm, "end": v(23.2, -4.84) * mm});
            skArc(sketch, "E52.21.11", {"start": v(26.23, -6.8) * mm, "mid": v(26.22, -6.57) * mm, "end": v(26.11, -6.37) * mm});
            skLineSegment(sketch, "E52.21.12", {"start": v(26.12, -7.22) * mm, "end": v(26.19, -7.02) * mm});
            skLineSegment(sketch, "E52.21.13", {"start": v(26.23, -6.8) * mm, "end": v(26.19, -7.02) * mm});
            skPoint(sketch, "E52.22.0", {"position": v(27.07, -0.96) * mm});
            skArc(sketch, "E52.22.1", {"start": v(25.56, -2.57) * mm, "mid": v(26.2, -2.32) * mm, "end": v(26.8, -2.02) * mm});
            skLineSegment(sketch, "E52.22.2", {"start": v(25, -2.64) * mm, "end": v(23.56, -2.57) * mm});
            skPoint(sketch, "E52.22.3", {"position": v(25.26, -2.66) * mm});
            skPoint(sketch, "E52.22.4", {"position": v(25.4, 0) * mm});
            skArc(sketch, "E52.22.5", {"start": v(25.69, -0.12) * mm, "mid": v(26.3, -0.43) * mm, "end": v(26.86, -0.8) * mm});
            skPoint(sketch, "E52.22.6", {"position": v(27.02, -1.88) * mm});
            skArc(sketch, "E52.22.7", {"start": v(26.8, -2.02) * mm, "mid": v(26.97, -1.85) * mm, "end": v(27.05, -1.63) * mm});
            skArc(sketch, "E52.22.8", {"start": v(25.69, -0.12) * mm, "mid": v(25.42, -0.03) * mm, "end": v(25.13, 0.01) * mm});
            skArc(sketch, "E52.22.9", {"start": v(25, -2.64) * mm, "mid": v(25.28, -2.63) * mm, "end": v(25.56, -2.57) * mm});
            skLineSegment(sketch, "E52.22.10", {"start": v(25.13, 0.01) * mm, "end": v(23.7, 0.09) * mm});
            skArc(sketch, "E52.22.11", {"start": v(27.07, -1.2) * mm, "mid": v(27.02, -0.98) * mm, "end": v(26.86, -0.8) * mm});
            skLineSegment(sketch, "E52.22.12", {"start": v(27.05, -1.63) * mm, "end": v(27.07, -1.42) * mm});
            skLineSegment(sketch, "E52.22.13", {"start": v(27.07, -1.2) * mm, "end": v(27.07, -1.42) * mm});
            skPoint(sketch, "E52.23.0", {"position": v(26.68, 4.7) * mm});
            skArc(sketch, "E52.23.1", {"start": v(25.54, 2.8) * mm, "mid": v(26.1, 3.17) * mm, "end": v(26.63, 3.6) * mm});
            skLineSegment(sketch, "E52.23.2", {"start": v(25, 2.61) * mm, "end": v(23.58, 2.39) * mm});
            skPoint(sketch, "E52.23.3", {"position": v(25.26, 2.66) * mm});
            skPoint(sketch, "E52.23.4", {"position": v(24.84, 5.28) * mm});
            skArc(sketch, "E52.23.5", {"start": v(25.15, 5.22) * mm, "mid": v(25.8, 5.05) * mm, "end": v(26.44, 4.8) * mm});
            skPoint(sketch, "E52.23.6", {"position": v(26.82, 3.78) * mm});
            skArc(sketch, "E52.23.7", {"start": v(26.63, 3.6) * mm, "mid": v(26.77, 3.8) * mm, "end": v(26.8, 4.03) * mm});
            skArc(sketch, "E52.23.8", {"start": v(25.15, 5.22) * mm, "mid": v(24.87, 5.26) * mm, "end": v(24.58, 5.24) * mm});
            skArc(sketch, "E52.23.9", {"start": v(25, 2.61) * mm, "mid": v(25.27, 2.68) * mm, "end": v(25.54, 2.8) * mm});
            skLineSegment(sketch, "E52.23.10", {"start": v(24.58, 5.24) * mm, "end": v(23.16, 5.01) * mm});
            skArc(sketch, "E52.23.11", {"start": v(26.73, 4.45) * mm, "mid": v(26.63, 4.66) * mm, "end": v(26.44, 4.8) * mm});
            skLineSegment(sketch, "E52.23.12", {"start": v(26.8, 4.03) * mm, "end": v(26.78, 4.24) * mm});
            skLineSegment(sketch, "E52.23.13", {"start": v(26.73, 4.45) * mm, "end": v(26.78, 4.24) * mm});
            skPoint(sketch, "E52.24.0", {"position": v(25.12, 10.14) * mm});
            skArc(sketch, "E52.24.1", {"start": v(24.4, 8.05) * mm, "mid": v(24.88, 8.53) * mm, "end": v(25.3, 9.06) * mm});
            skLineSegment(sketch, "E52.24.2", {"start": v(23.9, 7.75) * mm, "end": v(22.57, 7.24) * mm});
            skPoint(sketch, "E52.24.3", {"position": v(24.16, 7.85) * mm});
            skPoint(sketch, "E52.24.4", {"position": v(23.2, 10.33) * mm});
            skArc(sketch, "E52.24.5", {"start": v(23.52, 10.34) * mm, "mid": v(24.2, 10.3) * mm, "end": v(24.87, 10.2) * mm});
            skPoint(sketch, "E52.24.6", {"position": v(25.45, 9.28) * mm});
            skArc(sketch, "E52.24.7", {"start": v(25.3, 9.06) * mm, "mid": v(25.4, 9.28) * mm, "end": v(25.37, 9.51) * mm});
            skArc(sketch, "E52.24.8", {"start": v(23.52, 10.34) * mm, "mid": v(23.23, 10.31) * mm, "end": v(22.95, 10.23) * mm});
            skArc(sketch, "E52.24.9", {"start": v(23.9, 7.75) * mm, "mid": v(24.16, 7.88) * mm, "end": v(24.4, 8.05) * mm});
            skLineSegment(sketch, "E52.24.10", {"start": v(22.95, 10.23) * mm, "end": v(21.61, 9.72) * mm});
            skArc(sketch, "E52.24.11", {"start": v(25.22, 9.9) * mm, "mid": v(25.08, 10.1) * mm, "end": v(24.87, 10.2) * mm});
            skLineSegment(sketch, "E52.24.12", {"start": v(25.37, 9.51) * mm, "end": v(25.3, 9.72) * mm});
            skLineSegment(sketch, "E52.24.13", {"start": v(25.22, 9.9) * mm, "end": v(25.3, 9.72) * mm});
            skPoint(sketch, "E52.25.0", {"position": v(22.46, 15.14) * mm});
            skArc(sketch, "E52.25.1", {"start": v(22.19, 12.95) * mm, "mid": v(22.56, 13.52) * mm, "end": v(22.87, 14.12) * mm});
            skLineSegment(sketch, "E52.25.2", {"start": v(21.77, 12.55) * mm, "end": v(20.57, 11.77) * mm});
            skPoint(sketch, "E52.25.3", {"position": v(22, 12.7) * mm});
            skPoint(sketch, "E52.25.4", {"position": v(20.55, 14.93) * mm});
            skArc(sketch, "E52.25.5", {"start": v(20.85, 15) * mm, "mid": v(21.52, 15.11) * mm, "end": v(22.2, 15.15) * mm});
            skPoint(sketch, "E52.25.6", {"position": v(22.97, 14.36) * mm});
            skArc(sketch, "E52.25.7", {"start": v(22.87, 14.12) * mm, "mid": v(22.9, 14.36) * mm, "end": v(22.84, 14.58) * mm});
            skArc(sketch, "E52.25.8", {"start": v(20.85, 15) * mm, "mid": v(20.58, 14.92) * mm, "end": v(20.32, 14.78) * mm});
            skArc(sketch, "E52.25.9", {"start": v(21.77, 12.55) * mm, "mid": v(22, 12.73) * mm, "end": v(22.19, 12.95) * mm});
            skLineSegment(sketch, "E52.25.10", {"start": v(20.32, 14.78) * mm, "end": v(19.12, 14) * mm});
            skArc(sketch, "E52.25.11", {"start": v(22.61, 14.94) * mm, "mid": v(22.43, 15.09) * mm, "end": v(22.2, 15.15) * mm});
            skLineSegment(sketch, "E52.25.12", {"start": v(22.84, 14.58) * mm, "end": v(22.74, 14.76) * mm});
            skLineSegment(sketch, "E52.25.13", {"start": v(22.61, 14.94) * mm, "end": v(22.74, 14.76) * mm});
            skPoint(sketch, "E52.26.0", {"position": v(18.83, 19.48) * mm});
            skArc(sketch, "E52.26.1", {"start": v(19.01, 17.28) * mm, "mid": v(19.25, 17.91) * mm, "end": v(19.43, 18.57) * mm});
            skLineSegment(sketch, "E52.26.2", {"start": v(18.68, 16.8) * mm, "end": v(17.67, 15.8) * mm});
            skPoint(sketch, "E52.26.3", {"position": v(18.88, 17) * mm});
            skPoint(sketch, "E52.26.4", {"position": v(17, 18.88) * mm});
            skArc(sketch, "E52.26.5", {"start": v(17.28, 19.01) * mm, "mid": v(17.91, 19.25) * mm, "end": v(18.57, 19.43) * mm});
            skPoint(sketch, "E52.26.6", {"position": v(19.48, 18.83) * mm});
            skArc(sketch, "E52.26.7", {"start": v(19.43, 18.57) * mm, "mid": v(19.42, 18.8) * mm, "end": v(19.31, 19.01) * mm});
            skArc(sketch, "E52.26.8", {"start": v(17.28, 19.01) * mm, "mid": v(17.03, 18.87) * mm, "end": v(16.8, 18.68) * mm});
            skArc(sketch, "E52.26.9", {"start": v(18.68, 16.8) * mm, "mid": v(18.87, 17.03) * mm, "end": v(19.01, 17.28) * mm});
            skLineSegment(sketch, "E52.26.10", {"start": v(16.8, 18.68) * mm, "end": v(15.8, 17.67) * mm});
            skArc(sketch, "E52.26.11", {"start": v(19.01, 19.31) * mm, "mid": v(18.8, 19.42) * mm, "end": v(18.57, 19.43) * mm});
            skLineSegment(sketch, "E52.26.12", {"start": v(19.31, 19.01) * mm, "end": v(19.17, 19.17) * mm});
            skLineSegment(sketch, "E52.26.13", {"start": v(19.01, 19.31) * mm, "end": v(19.17, 19.17) * mm});
            skPoint(sketch, "E52.27.0", {"position": v(14.36, 22.97) * mm});
            skArc(sketch, "E52.27.1", {"start": v(15, 20.85) * mm, "mid": v(15.11, 21.52) * mm, "end": v(15.15, 22.2) * mm});
            skLineSegment(sketch, "E52.27.2", {"start": v(14.78, 20.32) * mm, "end": v(14, 19.12) * mm});
            skPoint(sketch, "E52.27.3", {"position": v(14.93, 20.55) * mm});
            skPoint(sketch, "E52.27.4", {"position": v(12.7, 22) * mm});
            skArc(sketch, "E52.27.5", {"start": v(12.95, 22.19) * mm, "mid": v(13.52, 22.56) * mm, "end": v(14.12, 22.87) * mm});
            skPoint(sketch, "E52.27.6", {"position": v(15.14, 22.46) * mm});
            skArc(sketch, "E52.27.7", {"start": v(15.15, 22.2) * mm, "mid": v(15.09, 22.43) * mm, "end": v(14.94, 22.61) * mm});
            skArc(sketch, "E52.27.8", {"start": v(12.95, 22.19) * mm, "mid": v(12.73, 22) * mm, "end": v(12.55, 21.77) * mm});
            skArc(sketch, "E52.27.9", {"start": v(14.78, 20.32) * mm, "mid": v(14.92, 20.58) * mm, "end": v(15, 20.85) * mm});
            skLineSegment(sketch, "E52.27.10", {"start": v(12.55, 21.77) * mm, "end": v(11.77, 20.57) * mm});
            skArc(sketch, "E52.27.11", {"start": v(14.58, 22.84) * mm, "mid": v(14.36, 22.9) * mm, "end": v(14.12, 22.87) * mm});
            skLineSegment(sketch, "E52.27.12", {"start": v(14.94, 22.61) * mm, "end": v(14.76, 22.74) * mm});
            skLineSegment(sketch, "E52.27.13", {"start": v(14.58, 22.84) * mm, "end": v(14.76, 22.74) * mm});
            skPoint(sketch, "E52.28.0", {"position": v(9.28, 25.45) * mm});
            skArc(sketch, "E52.28.1", {"start": v(10.34, 23.52) * mm, "mid": v(10.3, 24.2) * mm, "end": v(10.2, 24.87) * mm});
            skLineSegment(sketch, "E52.28.2", {"start": v(10.23, 22.95) * mm, "end": v(9.72, 21.61) * mm});
            skPoint(sketch, "E52.28.3", {"position": v(10.33, 23.2) * mm});
            skPoint(sketch, "E52.28.4", {"position": v(7.85, 24.16) * mm});
            skArc(sketch, "E52.28.5", {"start": v(8.05, 24.4) * mm, "mid": v(8.53, 24.88) * mm, "end": v(9.06, 25.3) * mm});
            skPoint(sketch, "E52.28.6", {"position": v(10.14, 25.12) * mm});
            skArc(sketch, "E52.28.7", {"start": v(10.2, 24.87) * mm, "mid": v(10.1, 25.08) * mm, "end": v(9.9, 25.22) * mm});
            skArc(sketch, "E52.28.8", {"start": v(8.05, 24.4) * mm, "mid": v(7.88, 24.16) * mm, "end": v(7.75, 23.9) * mm});
            skArc(sketch, "E52.28.9", {"start": v(10.23, 22.95) * mm, "mid": v(10.31, 23.23) * mm, "end": v(10.34, 23.52) * mm});
            skLineSegment(sketch, "E52.28.10", {"start": v(7.75, 23.9) * mm, "end": v(7.24, 22.57) * mm});
            skArc(sketch, "E52.28.11", {"start": v(9.51, 25.37) * mm, "mid": v(9.28, 25.4) * mm, "end": v(9.06, 25.3) * mm});
            skLineSegment(sketch, "E52.28.12", {"start": v(9.9, 25.22) * mm, "end": v(9.72, 25.3) * mm});
            skLineSegment(sketch, "E52.28.13", {"start": v(9.51, 25.37) * mm, "end": v(9.72, 25.3) * mm});
            skPoint(sketch, "E52.29.0", {"position": v(3.78, 26.82) * mm});
            skArc(sketch, "E52.29.1", {"start": v(5.22, 25.15) * mm, "mid": v(5.05, 25.8) * mm, "end": v(4.8, 26.44) * mm});
            skLineSegment(sketch, "E52.29.2", {"start": v(5.24, 24.58) * mm, "end": v(5.01, 23.16) * mm});
            skPoint(sketch, "E52.29.3", {"position": v(5.28, 24.84) * mm});
            skPoint(sketch, "E52.29.4", {"position": v(2.66, 25.26) * mm});
            skArc(sketch, "E52.29.5", {"start": v(2.8, 25.54) * mm, "mid": v(3.17, 26.1) * mm, "end": v(3.6, 26.63) * mm});
            skPoint(sketch, "E52.29.6", {"position": v(4.7, 26.68) * mm});
            skArc(sketch, "E52.29.7", {"start": v(4.8, 26.44) * mm, "mid": v(4.66, 26.63) * mm, "end": v(4.45, 26.73) * mm});
            skArc(sketch, "E52.29.8", {"start": v(2.8, 25.54) * mm, "mid": v(2.68, 25.27) * mm, "end": v(2.61, 25) * mm});
            skArc(sketch, "E52.29.9", {"start": v(5.24, 24.58) * mm, "mid": v(5.26, 24.87) * mm, "end": v(5.22, 25.15) * mm});
            skLineSegment(sketch, "E52.29.10", {"start": v(2.61, 25) * mm, "end": v(2.39, 23.58) * mm});
            skArc(sketch, "E52.29.11", {"start": v(4.03, 26.8) * mm, "mid": v(3.8, 26.77) * mm, "end": v(3.6, 26.63) * mm});
            skLineSegment(sketch, "E52.29.12", {"start": v(4.45, 26.73) * mm, "end": v(4.24, 26.78) * mm});
            skLineSegment(sketch, "E52.29.13", {"start": v(4.03, 26.8) * mm, "end": v(4.24, 26.78) * mm});
            skArc(sketch, "E53.trimOffspring", {"start": v(-7.4, 22.51) * mm, "mid": v(-8.5, 22.12) * mm, "end": v(-9.56, 21.69) * mm});
            skArc(sketch, "E54.trimOffspring", {"start": v(-11.93, 20.48) * mm, "mid": v(-12.9, 19.87) * mm, "end": v(-13.86, 19.22) * mm});
            skArc(sketch, "E55.trimOffspring", {"start": v(-15.92, 17.55) * mm, "mid": v(-16.76, 16.76) * mm, "end": v(-17.55, 15.92) * mm});
            skArc(sketch, "E56.trimOffspring", {"start": v(-19.22, 13.86) * mm, "mid": v(-19.87, 12.9) * mm, "end": v(-20.48, 11.93) * mm});
            skArc(sketch, "E57.trimOffspring", {"start": v(-21.69, 9.56) * mm, "mid": v(-22.12, 8.5) * mm, "end": v(-22.51, 7.4) * mm});
            skArc(sketch, "E58.trimOffspring", {"start": v(-23.2, 4.84) * mm, "mid": v(-23.4, 3.7) * mm, "end": v(-23.56, 2.57) * mm});
            skArc(sketch, "E59.trimOffspring", {"start": v(-23.7, -0.09) * mm, "mid": v(-23.67, -1.24) * mm, "end": v(-23.58, -2.39) * mm});
            skArc(sketch, "E60.trimOffspring", {"start": v(-23.16, -5.01) * mm, "mid": v(-22.9, -6.13) * mm, "end": v(-22.57, -7.24) * mm});
            skArc(sketch, "E61.trimOffspring", {"start": v(-21.61, -9.72) * mm, "mid": v(-21.12, -10.76) * mm, "end": v(-20.57, -11.77) * mm});
            skArc(sketch, "E62.trimOffspring", {"start": v(-19.12, -14) * mm, "mid": v(-18.42, -14.91) * mm, "end": v(-17.67, -15.8) * mm});
            skArc(sketch, "E63.trimOffspring", {"start": v(-15.8, -17.67) * mm, "mid": v(-14.91, -18.42) * mm, "end": v(-14, -19.12) * mm});
            skArc(sketch, "E64.trimOffspring", {"start": v(-11.77, -20.57) * mm, "mid": v(-10.76, -21.12) * mm, "end": v(-9.72, -21.61) * mm});
            skArc(sketch, "E65.trimOffspring", {"start": v(-7.24, -22.57) * mm, "mid": v(-6.13, -22.9) * mm, "end": v(-5.01, -23.16) * mm});
            skArc(sketch, "E66.trimOffspring", {"start": v(-2.39, -23.58) * mm, "mid": v(-1.24, -23.67) * mm, "end": v(-0.09, -23.7) * mm});
            skArc(sketch, "E67.trimOffspring", {"start": v(2.57, -23.56) * mm, "mid": v(3.7, -23.4) * mm, "end": v(4.84, -23.2) * mm});
            skArc(sketch, "E68.trimOffspring", {"start": v(7.4, -22.51) * mm, "mid": v(8.5, -22.12) * mm, "end": v(9.56, -21.69) * mm});
            skArc(sketch, "E69.trimOffspring", {"start": v(11.93, -20.48) * mm, "mid": v(12.9, -19.87) * mm, "end": v(13.86, -19.22) * mm});
            skArc(sketch, "E70.trimOffspring", {"start": v(15.92, -17.55) * mm, "mid": v(16.76, -16.76) * mm, "end": v(17.55, -15.92) * mm});
            skArc(sketch, "E71.trimOffspring", {"start": v(19.22, -13.86) * mm, "mid": v(19.87, -12.9) * mm, "end": v(20.48, -11.93) * mm});
            skArc(sketch, "E72.trimOffspring", {"start": v(21.69, -9.56) * mm, "mid": v(22.12, -8.5) * mm, "end": v(22.51, -7.4) * mm});
            skArc(sketch, "E73.trimOffspring", {"start": v(23.2, -4.84) * mm, "mid": v(23.4, -3.7) * mm, "end": v(23.56, -2.57) * mm});
            skArc(sketch, "E74.trimOffspring", {"start": v(23.7, 0.09) * mm, "mid": v(23.67, 1.24) * mm, "end": v(23.58, 2.39) * mm});
            skArc(sketch, "E75.trimOffspring", {"start": v(23.16, 5.01) * mm, "mid": v(22.9, 6.13) * mm, "end": v(22.57, 7.24) * mm});
            skArc(sketch, "E76.trimOffspring", {"start": v(21.61, 9.72) * mm, "mid": v(21.12, 10.76) * mm, "end": v(20.57, 11.77) * mm});
            skArc(sketch, "E77.trimOffspring", {"start": v(19.12, 14) * mm, "mid": v(18.42, 14.91) * mm, "end": v(17.67, 15.8) * mm});
            skArc(sketch, "E78.trimOffspring", {"start": v(15.8, 17.67) * mm, "mid": v(14.91, 18.42) * mm, "end": v(14, 19.12) * mm});
            skArc(sketch, "E79.trimOffspring", {"start": v(11.77, 20.57) * mm, "mid": v(10.76, 21.12) * mm, "end": v(9.72, 21.61) * mm});
            skArc(sketch, "E80.trimOffspring", {"start": v(7.24, 22.57) * mm, "mid": v(6.13, 22.9) * mm, "end": v(5.01, 23.16) * mm});
            skArc(sketch, "E81.trimOffspring", {"start": v(2.39, 23.58) * mm, "mid": v(1.24, 23.67) * mm, "end": v(0.09, 23.7) * mm});
            skSolve(sketch);
        }
        {
            var Q0;
            Q0=qSketchRegion(id+"F2",true);
            var Q1;
            Q1=qSketchRegion(id+"F1",true);
            var Q2;
            Q2=sQuery(id+"F2.wireOp",VERTEX,"E43.end");
            var Q3;
            Q3=sQuery(id+"F1.wireOp",VERTEX,"E0.end");
            loft(context, id + "F3", {"sheetProfilesArray" : [{ "sheetProfileEntities" : qUnion([Q0]) }, { "sheetProfileEntities" : qUnion([Q1]) }], "matchConnections" : true, "connections" : [{ "connectionEntities" : qUnion([Q2, Q3]), "connectionEdgeQueries" : qUnion([]), "connectionEdgeParameters" : [] }]});
        }
        {
            var Q0;
            Q0=sQuery(id+"F1.wireOp",VERTEX,"E0.center");
            var Q1;
            Q1=makeQuery(id+"F3.opLoft","SWEPT_BODY",BODY,{"disambiguationData":[OSD([makeQuery(id+"F1.imprint","IMPRINT",FACE,{"disambiguationData":[TD([[makeQuery(id+"F1.imprint","IMPRINT",EDGE,{"derivedFrom":sQuery(id+"F1.wireOp",EDGE,"E0")}),1.0]])]}),makeQuery(id+"F2.imprint","IMPRINT",FACE,{"disambiguationData":[TD([[makeQuery(id+"F2.imprint","IMPRINT",EDGE,{"derivedFrom":sQuery(id+"F2.wireOp",EDGE,"E41")}),1.0]])]})])]});
            hole(context, id + "F4", {"style" : HoleStyle.SIMPLE, "endStyle" : HoleEndStyle.BLIND, "oppositeDirection" : true, "holeDiameter" : 12.7 * mm, "holeDepth" : 50.8 * mm, "tappedDepth" : 12.7 * mm, "tapClearance" : 3, "locations" : qUnion([Q0]), "scope" : qUnion([Q1])});
        }
    });
